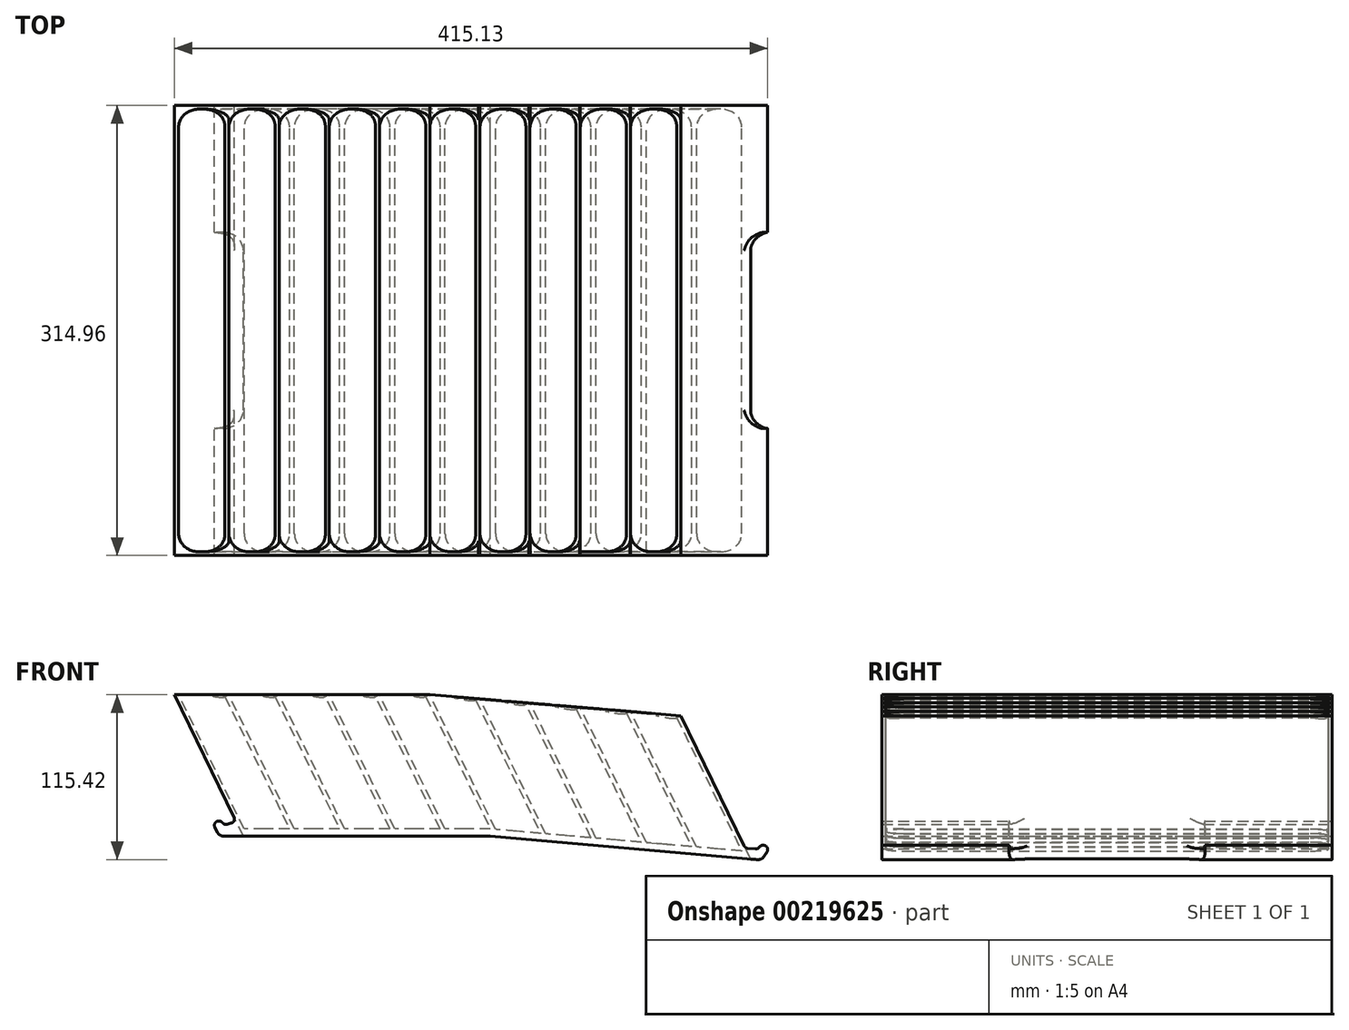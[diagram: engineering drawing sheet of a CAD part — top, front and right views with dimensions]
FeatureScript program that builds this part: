
annotation { "Feature Type Name" : "Feature", "Feature Type Description" : "" }
export const myFeature = defineFeature(function(context is Context, id is Id, definition is map)
    precondition{}
    {
        {
            var Q0;
            Q0=qCreatedBy(makeId("Front.planeOp"),FACE);
            var sketch = newSketch(context, id + "F0", { "sketchPlane" : qUnion([Q0])});
            skLineSegment(sketch, "E0", {"start": v(0, 0) * mm, "end": v(189.48, 0) * mm});
            skLineSegment(sketch, "E1", {"start": v(189.48, 0) * mm, "end": v(379.26, -16.6) * mm});
            skLineSegment(sketch, "E2", {"start": v(367.73, -8.25) * mm, "end": v(332.9, 63.16) * mm});
            skLineSegment(sketch, "E3", {"start": v(332.9, 63.16) * mm, "end": v(330.16, 61.83) * mm, "construction": true});
            skLineSegment(sketch, "E4", {"start": v(330.16, 61.83) * mm, "end": v(365.33, -10.29) * mm});
            skLineSegment(sketch, "E5", {"start": v(11.64, 10.16) * mm, "end": v(-21.71, 78.55) * mm});
            skLineSegment(sketch, "E6", {"start": v(-21.71, 78.55) * mm, "end": v(-18.66, 78.55) * mm});
            skLineSegment(sketch, "E7", {"start": v(-18.66, 78.55) * mm, "end": v(17.17, 5.08) * mm});
            skLineSegment(sketch, "E8", {"start": v(17.17, 5.08) * mm, "end": v(48.92, 5.08) * mm});
            skLineSegment(sketch, "E9", {"start": v(48.92, 5.08) * mm, "end": v(13.74, 77.21) * mm});
            skLineSegment(sketch, "E10", {"start": v(13.74, 77.21) * mm, "end": v(16.48, 78.55) * mm});
            skLineSegment(sketch, "E11", {"start": v(16.48, 78.55) * mm, "end": v(52.31, 5.08) * mm});
            skLineSegment(sketch, "E12", {"start": v(52.31, 5.08) * mm, "end": v(84.06, 5.08) * mm});
            skLineSegment(sketch, "E13", {"start": v(84.06, 5.08) * mm, "end": v(48.88, 77.21) * mm});
            skLineSegment(sketch, "E14", {"start": v(48.88, 77.21) * mm, "end": v(51.62, 78.55) * mm, "construction": true});
            skLineSegment(sketch, "E15", {"start": v(51.62, 78.55) * mm, "end": v(87.45, 5.08) * mm});
            skLineSegment(sketch, "E16", {"start": v(87.45, 5.08) * mm, "end": v(119.2, 5.08) * mm});
            skLineSegment(sketch, "E17", {"start": v(119.2, 5.08) * mm, "end": v(84.02, 77.21) * mm});
            skLineSegment(sketch, "E18", {"start": v(86.76, 78.55) * mm, "end": v(122.6, 5.08) * mm});
            skLineSegment(sketch, "E19", {"start": v(122.6, 5.08) * mm, "end": v(154.34, 5.08) * mm});
            skLineSegment(sketch, "E20", {"start": v(154.34, 5.08) * mm, "end": v(119.16, 77.21) * mm});
            skLineSegment(sketch, "E21", {"start": v(119.16, 77.21) * mm, "end": v(121.9, 78.55) * mm, "construction": true});
            skLineSegment(sketch, "E22", {"start": v(121.9, 78.55) * mm, "end": v(157.73, 5.08) * mm});
            skLineSegment(sketch, "E23", {"start": v(157.73, 5.08) * mm, "end": v(189.48, 5.08) * mm});
            skLineSegment(sketch, "E24", {"start": v(189.48, 0) * mm, "end": v(189.48, 5.08) * mm, "construction": true});
            skLineSegment(sketch, "E25", {"start": v(189.48, 5.08) * mm, "end": v(154.3, 77.21) * mm});
            skLineSegment(sketch, "E26", {"start": v(154.3, 77.21) * mm, "end": v(157.04, 78.55) * mm, "construction": true});
            skLineSegment(sketch, "E27", {"start": v(157.04, 78.55) * mm, "end": v(193.02, 4.8) * mm});
            skLineSegment(sketch, "E28", {"start": v(193.02, 4.8) * mm, "end": v(224.65, 2.02) * mm});
            skLineSegment(sketch, "E29", {"start": v(224.65, 2.02) * mm, "end": v(189.47, 74.14) * mm});
            skLineSegment(sketch, "E30", {"start": v(189.47, 74.14) * mm, "end": v(192.21, 75.47) * mm, "construction": true});
            skLineSegment(sketch, "E31", {"start": v(192.21, 75.47) * mm, "end": v(228.19, 1.71) * mm});
            skLineSegment(sketch, "E32", {"start": v(224.65, 2.02) * mm, "end": v(228.19, 1.71) * mm, "construction": true});
            skLineSegment(sketch, "E33", {"start": v(228.19, 1.71) * mm, "end": v(259.82, -1.05) * mm});
            skLineSegment(sketch, "E34", {"start": v(259.82, -1.05) * mm, "end": v(224.65, 71.06) * mm});
            skLineSegment(sketch, "E35", {"start": v(224.65, 71.06) * mm, "end": v(227.39, 72.4) * mm, "construction": true});
            skLineSegment(sketch, "E36", {"start": v(227.39, 72.4) * mm, "end": v(263.36, -1.36) * mm});
            skLineSegment(sketch, "E37", {"start": v(263.36, -1.36) * mm, "end": v(294.99, -4.13) * mm});
            skLineSegment(sketch, "E38", {"start": v(294.99, -4.13) * mm, "end": v(259.82, 67.98) * mm});
            skLineSegment(sketch, "E39", {"start": v(259.82, 67.98) * mm, "end": v(262.56, 69.32) * mm, "construction": true});
            skLineSegment(sketch, "E40", {"start": v(262.56, 69.32) * mm, "end": v(298.53, -4.44) * mm});
            skLineSegment(sketch, "E41", {"start": v(298.53, -4.44) * mm, "end": v(330.16, -7.2) * mm});
            skLineSegment(sketch, "E42", {"start": v(330.16, -7.2) * mm, "end": v(294.99, 64.9) * mm});
            skLineSegment(sketch, "E43", {"start": v(294.99, 64.9) * mm, "end": v(297.73, 66.24) * mm, "construction": true});
            skLineSegment(sketch, "E44", {"start": v(297.73, 66.24) * mm, "end": v(333.7, -7.52) * mm});
            skLineSegment(sketch, "E45", {"start": v(333.7, -7.52) * mm, "end": v(365.33, -10.29) * mm});
            skLineSegment(sketch, "E46", {"start": v(-18.66, 78.55) * mm, "end": v(157.04, 78.55) * mm, "construction": true});
            skLineSegment(sketch, "E47", {"start": v(157.04, 78.55) * mm, "end": v(332.9, 63.16) * mm, "construction": true});
            skLineSegment(sketch, "E48", {"start": v(84.02, 77.21) * mm, "end": v(86.76, 78.55) * mm, "construction": true});
            skLineSegment(sketch, "E49", {"start": v(367.73, -8.25) * mm, "end": v(376.94, -9.06) * mm});
            skLineSegment(sketch, "E50", {"start": v(379.26, -16.6) * mm, "end": v(383.77, -9.65) * mm});
            skArc(sketch, "E51", {"start": v(383.77, -9.65) * mm, "mid": v(380.63, -6.27) * mm, "end": v(376.94, -9.06) * mm});
            skLineSegment(sketch, "E52", {"start": v(376.94, -9.06) * mm, "end": v(383.77, -9.65) * mm, "construction": true});
            skLineSegment(sketch, "E53", {"start": v(0, 0) * mm, "end": v(-4.05, 7.62) * mm});
            skLineSegment(sketch, "E54", {"start": v(11.64, 10.16) * mm, "end": v(2.8, 7.62) * mm});
            skArc(sketch, "E55", {"start": v(2.8, 7.62) * mm, "mid": v(-0.62, 10.67) * mm, "end": v(-4.05, 7.62) * mm});
            skLineSegment(sketch, "E56", {"start": v(-4.05, 7.62) * mm, "end": v(2.8, 7.62) * mm, "construction": true});
            skLineSegment(sketch, "E57", {"start": v(-21.71, 78.55) * mm, "end": v(-31.72, 99.06) * mm});
            skLineSegment(sketch, "E58", {"start": v(-31.72, 99.06) * mm, "end": v(-28.67, 99.06) * mm});
            skLineSegment(sketch, "E59", {"start": v(-28.67, 99.06) * mm, "end": v(-18.66, 78.55) * mm});
            skLineSegment(sketch, "E60", {"start": v(13.74, 77.21) * mm, "end": v(3.73, 97.72) * mm});
            skLineSegment(sketch, "E61", {"start": v(3.73, 97.72) * mm, "end": v(6.47, 99.06) * mm});
            skLineSegment(sketch, "E62", {"start": v(6.47, 99.06) * mm, "end": v(16.48, 78.55) * mm});
            skLineSegment(sketch, "E63", {"start": v(48.88, 77.21) * mm, "end": v(38.87, 97.72) * mm});
            skLineSegment(sketch, "E64", {"start": v(38.87, 97.72) * mm, "end": v(41.61, 99.06) * mm});
            skLineSegment(sketch, "E65", {"start": v(41.61, 99.06) * mm, "end": v(51.62, 78.55) * mm});
            skLineSegment(sketch, "E66", {"start": v(109.16, 97.72) * mm, "end": v(111.9, 99.06) * mm});
            skLineSegment(sketch, "E67", {"start": v(259.82, 67.98) * mm, "end": v(249.49, 89.16) * mm});
            skLineSegment(sketch, "E68", {"start": v(249.49, 89.16) * mm, "end": v(252.23, 90.5) * mm});
            skLineSegment(sketch, "E69", {"start": v(252.23, 90.5) * mm, "end": v(262.56, 69.32) * mm});
            skLineSegment(sketch, "E70", {"start": v(330.16, 61.83) * mm, "end": v(319.83, 83) * mm});
            skLineSegment(sketch, "E71", {"start": v(319.83, 83) * mm, "end": v(322.57, 84.34) * mm});
            skLineSegment(sketch, "E72", {"start": v(322.57, 84.34) * mm, "end": v(332.9, 63.16) * mm});
            skLineSegment(sketch, "E73", {"start": v(154.3, 77.21) * mm, "end": v(144.3, 97.72) * mm});
            skLineSegment(sketch, "E74", {"start": v(294.99, 64.9) * mm, "end": v(284.66, 86.08) * mm});
            skLineSegment(sketch, "E75", {"start": v(189.47, 74.14) * mm, "end": v(179.15, 95.31) * mm});
            skLineSegment(sketch, "E76", {"start": v(-28.67, 99.06) * mm, "end": v(154.3, 99.06) * mm, "construction": true});
            skLineSegment(sketch, "E77", {"start": v(322.57, 84.34) * mm, "end": v(154.3, 99.06) * mm, "construction": true});
            skLineSegment(sketch, "E78", {"start": v(86.76, 78.55) * mm, "end": v(76.76, 99.06) * mm});
            skLineSegment(sketch, "E79", {"start": v(76.76, 99.06) * mm, "end": v(74.02, 97.72) * mm});
            skLineSegment(sketch, "E80", {"start": v(74.02, 97.72) * mm, "end": v(84.02, 77.21) * mm});
            skLineSegment(sketch, "E81", {"start": v(109.16, 97.72) * mm, "end": v(119.16, 77.21) * mm});
            skLineSegment(sketch, "E82", {"start": v(111.9, 99.06) * mm, "end": v(121.9, 78.55) * mm});
            skLineSegment(sketch, "E83", {"start": v(157.04, 78.55) * mm, "end": v(147.04, 99.06) * mm});
            skLineSegment(sketch, "E84", {"start": v(147.04, 99.06) * mm, "end": v(144.3, 97.72) * mm});
            skLineSegment(sketch, "E85", {"start": v(192.21, 75.47) * mm, "end": v(181.89, 96.65) * mm});
            skLineSegment(sketch, "E86", {"start": v(181.89, 96.65) * mm, "end": v(179.15, 95.31) * mm});
            skLineSegment(sketch, "E87", {"start": v(227.39, 72.4) * mm, "end": v(217.06, 93.57) * mm});
            skLineSegment(sketch, "E88", {"start": v(217.06, 93.57) * mm, "end": v(214.32, 92.23) * mm});
            skLineSegment(sketch, "E89", {"start": v(214.32, 92.23) * mm, "end": v(224.65, 71.06) * mm});
            skLineSegment(sketch, "E90", {"start": v(297.73, 66.24) * mm, "end": v(287.4, 87.42) * mm});
            skLineSegment(sketch, "E91", {"start": v(287.4, 87.42) * mm, "end": v(284.66, 86.08) * mm});
            skSolve(sketch);
        }
        {
            var Q0;
            Q0 = qSketchRegion(id + "F0", true);
            extrude(context, id + "F1", {"entities" : qUnion([Q0]), "endBound" : BoundingType.SYMMETRIC, "depth" : 314.96 * mm});
        }
        {
            var Q0;
            Q0=makeQuery(id+"F1.opExtrude","SWEPT_EDGE",EDGE,{"disambiguationData":[OSD([sQuery(id+"F0.wireOp",EDGE,"E5"),sQuery(id+"F0.wireOp",EDGE,"E54")])]});
            var Q1;
            Q1=makeQuery(id+"F1.opExtrude","SWEPT_EDGE",EDGE,{"disambiguationData":[OSD([sQuery(id+"F0.wireOp",EDGE,"E54"),sQuery(id+"F0.wireOp",EDGE,"E55")])]});
            var Q2;
            Q2=makeQuery(id+"F1.opExtrude","SWEPT_EDGE",EDGE,{"disambiguationData":[OSD([sQuery(id+"F0.wireOp",EDGE,"E2"),sQuery(id+"F0.wireOp",EDGE,"E49")])]});
            var Q3;
            Q3=makeQuery(id+"F1.opExtrude","SWEPT_EDGE",EDGE,{"disambiguationData":[OSD([sQuery(id+"F0.wireOp",EDGE,"E49"),sQuery(id+"F0.wireOp",EDGE,"E51")])]});
            var Q4;
            Q4=makeQuery(id+"F1.opExtrude","SWEPT_EDGE",EDGE,{"disambiguationData":[OSD([sQuery(id+"F0.wireOp",EDGE,"E50"),sQuery(id+"F0.wireOp",EDGE,"E51")])]});
            var Q5;
            Q5=makeQuery(id+"F1.opExtrude","SWEPT_EDGE",EDGE,{"disambiguationData":[OSD([sQuery(id+"F0.wireOp",EDGE,"E53"),sQuery(id+"F0.wireOp",EDGE,"E55")])]});
            fillet(context, id + "F2", {"entities" : qUnion([Q0, Q1, Q2, Q3, Q4, Q5]), "radius" : 3.05 * mm, "tangentPropagation" : true, "allowEdgeOverflow" : false});
        }
        {
            var Q0;
            Q0=makeQuery(id+"F1.opExtrude","SWEPT_EDGE",EDGE,{"disambiguationData":[OSD([sQuery(id+"F0.wireOp",EDGE,"E0"),sQuery(id+"F0.wireOp",EDGE,"E53")])]});
            var Q1;
            Q1=makeQuery(id+"F1.opExtrude","SWEPT_EDGE",EDGE,{"disambiguationData":[OSD([sQuery(id+"F0.wireOp",EDGE,"E1"),sQuery(id+"F0.wireOp",EDGE,"E50")])]});
            fillet(context, id + "F3", {"entities" : qUnion([Q0, Q1]), "radius" : 5.08 * mm, "tangentPropagation" : true, "allowEdgeOverflow" : false});
        }
        {
            var Q0;
            Q0=makeQuery(id+"F1.opExtrude","CAP_FACE",FACE,{"disambiguationData":[OSD([sQuery(id+"F0.wireOp",EDGE,"E0"),sQuery(id+"F0.wireOp",EDGE,"E1"),sQuery(id+"F0.wireOp",EDGE,"E2"),sQuery(id+"F0.wireOp",EDGE,"E3"),sQuery(id+"F0.wireOp",EDGE,"E4"),sQuery(id+"F0.wireOp",EDGE,"E5"),sQuery(id+"F0.wireOp",EDGE,"E6"),sQuery(id+"F0.wireOp",EDGE,"E7"),sQuery(id+"F0.wireOp",EDGE,"E8"),sQuery(id+"F0.wireOp",EDGE,"E9"),sQuery(id+"F0.wireOp",EDGE,"E10"),sQuery(id+"F0.wireOp",EDGE,"E11"),sQuery(id+"F0.wireOp",EDGE,"E12"),sQuery(id+"F0.wireOp",EDGE,"E13"),sQuery(id+"F0.wireOp",EDGE,"E14"),sQuery(id+"F0.wireOp",EDGE,"E15"),sQuery(id+"F0.wireOp",EDGE,"E16"),sQuery(id+"F0.wireOp",EDGE,"E17"),sQuery(id+"F0.wireOp",EDGE,"E18"),sQuery(id+"F0.wireOp",EDGE,"E19"),sQuery(id+"F0.wireOp",EDGE,"E20"),sQuery(id+"F0.wireOp",EDGE,"E21"),sQuery(id+"F0.wireOp",EDGE,"E22"),sQuery(id+"F0.wireOp",EDGE,"E23"),sQuery(id+"F0.wireOp",EDGE,"E25"),sQuery(id+"F0.wireOp",EDGE,"E26"),sQuery(id+"F0.wireOp",EDGE,"E27"),sQuery(id+"F0.wireOp",EDGE,"E28"),sQuery(id+"F0.wireOp",EDGE,"E29"),sQuery(id+"F0.wireOp",EDGE,"E30"),sQuery(id+"F0.wireOp",EDGE,"E31"),sQuery(id+"F0.wireOp",EDGE,"E33"),sQuery(id+"F0.wireOp",EDGE,"E34"),sQuery(id+"F0.wireOp",EDGE,"E35"),sQuery(id+"F0.wireOp",EDGE,"E36"),sQuery(id+"F0.wireOp",EDGE,"E37"),sQuery(id+"F0.wireOp",EDGE,"E38"),sQuery(id+"F0.wireOp",EDGE,"E39"),sQuery(id+"F0.wireOp",EDGE,"E40"),sQuery(id+"F0.wireOp",EDGE,"E41"),sQuery(id+"F0.wireOp",EDGE,"E42"),sQuery(id+"F0.wireOp",EDGE,"E43"),sQuery(id+"F0.wireOp",EDGE,"E44"),sQuery(id+"F0.wireOp",EDGE,"E45"),sQuery(id+"F0.wireOp",EDGE,"E48"),sQuery(id+"F0.wireOp",EDGE,"E49"),sQuery(id+"F0.wireOp",EDGE,"E50"),sQuery(id+"F0.wireOp",EDGE,"E51"),sQuery(id+"F0.wireOp",EDGE,"E53"),sQuery(id+"F0.wireOp",EDGE,"E54"),sQuery(id+"F0.wireOp",EDGE,"E55")])],"isStart":false});
            var sketch = newSketch(context, id + "F4", { "sketchPlane" : qUnion([Q0])});
            skLineSegment(sketch, "E92.0", {"start": v(10.05, 13.42) * mm, "end": v(-31.72, 99.06) * mm});
            skArc(sketch, "E92.1", {"start": v(10.05, 13.42) * mm, "mid": v(10.1, 10.85) * mm, "end": v(8.15, 9.16) * mm});
            skLineSegment(sketch, "E92.2", {"start": v(8.15, 9.16) * mm, "end": v(5.3, 8.34) * mm});
            skArc(sketch, "E92.3", {"start": v(5.3, 8.34) * mm, "mid": v(3.53, 8.36) * mm, "end": v(2.08, 9.37) * mm});
            skArc(sketch, "E92.4", {"start": v(2.08, 9.37) * mm, "mid": v(0.97, 10.28) * mm, "end": v(-0.42, 10.66) * mm});
            skArc(sketch, "E92.5", {"start": v(-0.42, 10.66) * mm, "mid": v(-3.17, 9.26) * mm, "end": v(-3.3, 6.19) * mm});
            skLineSegment(sketch, "E92.6", {"start": v(-1.43, 2.7) * mm, "end": v(-3.3, 6.19) * mm});
            skArc(sketch, "E92.7", {"start": v(-1.43, 2.7) * mm, "mid": v(0.44, 0.73) * mm, "end": v(3.05, 0) * mm});
            skLineSegment(sketch, "E92.8", {"start": v(3.05, 0) * mm, "end": v(189.48, 0) * mm});
            skLineSegment(sketch, "E92.9", {"start": v(189.48, 0) * mm, "end": v(376.22, -16.34) * mm});
            skLineSegment(sketch, "E92.10", {"start": v(366.98, -6.7) * mm, "end": v(322.57, 84.34) * mm});
            skArc(sketch, "E92.11", {"start": v(369.45, -8.4) * mm, "mid": v(367.99, -7.88) * mm, "end": v(366.98, -6.7) * mm});
            skLineSegment(sketch, "E92.12", {"start": v(369.45, -8.4) * mm, "end": v(374.84, -8.87) * mm});
            skArc(sketch, "E92.13", {"start": v(377.56, -7.65) * mm, "mid": v(376.36, -8.62) * mm, "end": v(374.84, -8.87) * mm});
            skArc(sketch, "E92.14", {"start": v(380.66, -6.27) * mm, "mid": v(378.93, -6.55) * mm, "end": v(377.56, -7.65) * mm});
            skArc(sketch, "E92.15", {"start": v(382.92, -10.97) * mm, "mid": v(383.1, -7.98) * mm, "end": v(380.66, -6.27) * mm});
            skLineSegment(sketch, "E92.16", {"start": v(380.92, -14.04) * mm, "end": v(382.92, -10.97) * mm});
            skArc(sketch, "E92.17", {"start": v(376.22, -16.34) * mm, "mid": v(378.89, -15.84) * mm, "end": v(380.92, -14.04) * mm});
            skLineSegment(sketch, "E93", {"start": v(322.57, 84.34) * mm, "end": v(147.04, 99.06) * mm});
            skLineSegment(sketch, "E94", {"start": v(147.04, 99.06) * mm, "end": v(-31.72, 99.06) * mm});
            skSolve(sketch);
        }
        {
            var Q0;
            Q0 = qSketchRegion(id + "F4", true);
            extrude(context, id + "F5", {"entities" : qUnion([Q0]), "oppositeDirection" : true, "depth" : 2.54 * mm});
        }
        {
            var Q0;
            Q0=makeQuery(id+"F5.opExtrude","SWEPT_BODY",BODY,{"disambiguationData":[OSD([sQuery(id+"F4.wireOp",EDGE,"E92.0"),sQuery(id+"F4.wireOp",EDGE,"E92.1"),sQuery(id+"F4.wireOp",EDGE,"E92.2"),sQuery(id+"F4.wireOp",EDGE,"E92.3"),sQuery(id+"F4.wireOp",EDGE,"E92.4"),sQuery(id+"F4.wireOp",EDGE,"E92.5"),sQuery(id+"F4.wireOp",EDGE,"E92.6"),sQuery(id+"F4.wireOp",EDGE,"E92.7"),sQuery(id+"F4.wireOp",EDGE,"E92.8"),sQuery(id+"F4.wireOp",EDGE,"E92.9"),sQuery(id+"F4.wireOp",EDGE,"E92.10"),sQuery(id+"F4.wireOp",EDGE,"E92.11"),sQuery(id+"F4.wireOp",EDGE,"E92.12"),sQuery(id+"F4.wireOp",EDGE,"E92.13"),sQuery(id+"F4.wireOp",EDGE,"E92.14"),sQuery(id+"F4.wireOp",EDGE,"E92.15"),sQuery(id+"F4.wireOp",EDGE,"E92.16"),sQuery(id+"F4.wireOp",EDGE,"E92.17"),sQuery(id+"F4.wireOp",EDGE,"E93"),sQuery(id+"F4.wireOp",EDGE,"E94")])]});
            var Q1;
            Q1=qCreatedBy(makeId("Front.planeOp"),FACE);
            mirror(context, id + "F6", {"operationType" : NewBodyOperationType.ADD, "entities" : qUnion([Q0]), "mirrorPlane" : qUnion([Q1])});
        }
        {
            var Q0;
            Q0=makeQuery(id+"F1.opExtrude","SWEPT_FACE",FACE,{"disambiguationData":[OSD([sQuery(id+"F0.wireOp",EDGE,"E61")])]});
            var sketch = newSketch(context, id + "F7", { "sketchPlane" : qUnion([Q0])});
            skLineSegment(sketch, "E95.bottom", {"start": v(14.92, -68.58) * mm, "end": v(-14.92, -68.58) * mm});
            skLineSegment(sketch, "E95.top", {"start": v(14.92, 68.58) * mm, "end": v(-14.92, 68.58) * mm});
            skLineSegment(sketch, "E95.left", {"start": v(14.92, -68.58) * mm, "end": v(14.92, 68.58) * mm});
            skLineSegment(sketch, "E95.right", {"start": v(-14.92, -68.58) * mm, "end": v(-14.92, 68.58) * mm});
            skPoint(sketch, "E95.middle", {"position": v(0, 0) * mm});
            skSolve(sketch);
        }
        {
            var Q0;
            Q0 = qSketchRegion(id + "F7", true);
            extrude(context, id + "F8", {"entities" : qUnion([Q0]), "operationType" : NewBodyOperationType.REMOVE, "oppositeDirection" : true, "depth" : 144.78 * mm});
        }
        {
            var Q0;
            Q0=makeQuery(id+"F1.opExtrude","SWEPT_FACE",FACE,{"disambiguationData":[OSD([sQuery(id+"F0.wireOp",EDGE,"E61")])]});
            var sketch = newSketch(context, id + "F9", { "sketchPlane" : qUnion([Q0])});
            skLineSegment(sketch, "E96.bottom", {"start": v(326.9, -68.58) * mm, "end": v(466.95, -68.58) * mm});
            skLineSegment(sketch, "E96.top", {"start": v(326.9, 68.58) * mm, "end": v(466.95, 68.58) * mm});
            skLineSegment(sketch, "E96.left", {"start": v(326.9, -68.58) * mm, "end": v(326.9, 68.58) * mm});
            skLineSegment(sketch, "E96.right", {"start": v(466.95, -68.58) * mm, "end": v(466.95, 68.58) * mm});
            skPoint(sketch, "E96.middle", {"position": v(396.93, 0) * mm});
            skSolve(sketch);
        }
        {
            var Q0;
            Q0 = qSketchRegion(id + "F9", true);
            extrude(context, id + "F10", {"entities" : qUnion([Q0]), "operationType" : NewBodyOperationType.REMOVE, "oppositeDirection" : true, "depth" : 293.12 * mm});
        }
        {
            var Q0;
            Q0=makeQuery(id+"F10.boolean.opBoolean","COPY",EDGE,{"derivedFrom":makeQuery(id+"F10.opExtrude","SWEPT_EDGE",EDGE,{"disambiguationData":[OSD([sQuery(id+"F9.wireOp",EDGE,"E96.bottom"),sQuery(id+"F9.wireOp",EDGE,"E96.left")])]})});
            var Q1;
            Q1=makeQuery(id+"F10.boolean.opBoolean","COPY",EDGE,{"derivedFrom":makeQuery(id+"F10.opExtrude","SWEPT_EDGE",EDGE,{"disambiguationData":[OSD([sQuery(id+"F9.wireOp",EDGE,"E96.top"),sQuery(id+"F9.wireOp",EDGE,"E96.left")])]})});
            var Q2;
            Q2=makeQuery(id+"F8.boolean.opBoolean","COPY",EDGE,{"derivedFrom":makeQuery(id+"F8.opExtrude","SWEPT_EDGE",EDGE,{"disambiguationData":[OSD([sQuery(id+"F7.wireOp",EDGE,"E95.top"),sQuery(id+"F7.wireOp",EDGE,"E95.left")])]})});
            var Q3;
            Q3=makeQuery(id+"F8.boolean.opBoolean","COPY",EDGE,{"derivedFrom":makeQuery(id+"F8.opExtrude","SWEPT_EDGE",EDGE,{"disambiguationData":[OSD([sQuery(id+"F7.wireOp",EDGE,"E95.bottom"),sQuery(id+"F7.wireOp",EDGE,"E95.left")])]})});
            fillet(context, id + "F11", {"entities" : qUnion([Q0, Q1, Q2, Q3]), "radius" : 12.7 * mm, "tangentPropagation" : true, "allowEdgeOverflow" : false});
        }
        {
            var Q0;
            Q0=makeQuery(id+"F6.boolean.opBoolean","INTERSECT",EDGE,{"derivedFrom":[makeQuery(id+"F1.opExtrude","SWEPT_FACE",FACE,{"disambiguationData":[OSD([sQuery(id+"F0.wireOp",EDGE,"E29"),sQuery(id+"F0.wireOp",EDGE,"E75")])]}),makeQuery(id+"F5.opExtrude","CAP_FACE",FACE,{"disambiguationData":[OSD([sQuery(id+"F4.wireOp",EDGE,"E92.0"),sQuery(id+"F4.wireOp",EDGE,"E92.1"),sQuery(id+"F4.wireOp",EDGE,"E92.2"),sQuery(id+"F4.wireOp",EDGE,"E92.3"),sQuery(id+"F4.wireOp",EDGE,"E92.4"),sQuery(id+"F4.wireOp",EDGE,"E92.5"),sQuery(id+"F4.wireOp",EDGE,"E92.6"),sQuery(id+"F4.wireOp",EDGE,"E92.7"),sQuery(id+"F4.wireOp",EDGE,"E92.8"),sQuery(id+"F4.wireOp",EDGE,"E92.9"),sQuery(id+"F4.wireOp",EDGE,"E92.10"),sQuery(id+"F4.wireOp",EDGE,"E92.11"),sQuery(id+"F4.wireOp",EDGE,"E92.12"),sQuery(id+"F4.wireOp",EDGE,"E92.13"),sQuery(id+"F4.wireOp",EDGE,"E92.14"),sQuery(id+"F4.wireOp",EDGE,"E92.15"),sQuery(id+"F4.wireOp",EDGE,"E92.16"),sQuery(id+"F4.wireOp",EDGE,"E92.17"),sQuery(id+"F4.wireOp",EDGE,"E93"),sQuery(id+"F4.wireOp",EDGE,"E94")])],"isStart":false})]});
            var Q1;
            Q1=makeQuery(id+"F6.boolean.opBoolean","INTERSECT",EDGE,{"derivedFrom":[makeQuery(id+"F1.opExtrude","SWEPT_FACE",FACE,{"disambiguationData":[OSD([sQuery(id+"F0.wireOp",EDGE,"E27"),sQuery(id+"F0.wireOp",EDGE,"E83")])]}),makeQuery(id+"F5.opExtrude","CAP_FACE",FACE,{"disambiguationData":[OSD([sQuery(id+"F4.wireOp",EDGE,"E92.0"),sQuery(id+"F4.wireOp",EDGE,"E92.1"),sQuery(id+"F4.wireOp",EDGE,"E92.2"),sQuery(id+"F4.wireOp",EDGE,"E92.3"),sQuery(id+"F4.wireOp",EDGE,"E92.4"),sQuery(id+"F4.wireOp",EDGE,"E92.5"),sQuery(id+"F4.wireOp",EDGE,"E92.6"),sQuery(id+"F4.wireOp",EDGE,"E92.7"),sQuery(id+"F4.wireOp",EDGE,"E92.8"),sQuery(id+"F4.wireOp",EDGE,"E92.9"),sQuery(id+"F4.wireOp",EDGE,"E92.10"),sQuery(id+"F4.wireOp",EDGE,"E92.11"),sQuery(id+"F4.wireOp",EDGE,"E92.12"),sQuery(id+"F4.wireOp",EDGE,"E92.13"),sQuery(id+"F4.wireOp",EDGE,"E92.14"),sQuery(id+"F4.wireOp",EDGE,"E92.15"),sQuery(id+"F4.wireOp",EDGE,"E92.16"),sQuery(id+"F4.wireOp",EDGE,"E92.17"),sQuery(id+"F4.wireOp",EDGE,"E93"),sQuery(id+"F4.wireOp",EDGE,"E94")])],"isStart":false})]});
            var Q2;
            Q2=makeQuery(id+"F6.boolean.opBoolean","INTERSECT",EDGE,{"derivedFrom":[makeQuery(id+"F1.opExtrude","SWEPT_FACE",FACE,{"disambiguationData":[OSD([sQuery(id+"F0.wireOp",EDGE,"E25"),sQuery(id+"F0.wireOp",EDGE,"E73")])]}),makeQuery(id+"F5.opExtrude","CAP_FACE",FACE,{"disambiguationData":[OSD([sQuery(id+"F4.wireOp",EDGE,"E92.0"),sQuery(id+"F4.wireOp",EDGE,"E92.1"),sQuery(id+"F4.wireOp",EDGE,"E92.2"),sQuery(id+"F4.wireOp",EDGE,"E92.3"),sQuery(id+"F4.wireOp",EDGE,"E92.4"),sQuery(id+"F4.wireOp",EDGE,"E92.5"),sQuery(id+"F4.wireOp",EDGE,"E92.6"),sQuery(id+"F4.wireOp",EDGE,"E92.7"),sQuery(id+"F4.wireOp",EDGE,"E92.8"),sQuery(id+"F4.wireOp",EDGE,"E92.9"),sQuery(id+"F4.wireOp",EDGE,"E92.10"),sQuery(id+"F4.wireOp",EDGE,"E92.11"),sQuery(id+"F4.wireOp",EDGE,"E92.12"),sQuery(id+"F4.wireOp",EDGE,"E92.13"),sQuery(id+"F4.wireOp",EDGE,"E92.14"),sQuery(id+"F4.wireOp",EDGE,"E92.15"),sQuery(id+"F4.wireOp",EDGE,"E92.16"),sQuery(id+"F4.wireOp",EDGE,"E92.17"),sQuery(id+"F4.wireOp",EDGE,"E93"),sQuery(id+"F4.wireOp",EDGE,"E94")])],"isStart":false})]});
            var Q3;
            Q3=makeQuery(id+"F6.boolean.opBoolean","INTERSECT",EDGE,{"derivedFrom":[makeQuery(id+"F1.opExtrude","SWEPT_FACE",FACE,{"disambiguationData":[OSD([sQuery(id+"F0.wireOp",EDGE,"E22"),sQuery(id+"F0.wireOp",EDGE,"E82")])]}),makeQuery(id+"F5.opExtrude","CAP_FACE",FACE,{"disambiguationData":[OSD([sQuery(id+"F4.wireOp",EDGE,"E92.0"),sQuery(id+"F4.wireOp",EDGE,"E92.1"),sQuery(id+"F4.wireOp",EDGE,"E92.2"),sQuery(id+"F4.wireOp",EDGE,"E92.3"),sQuery(id+"F4.wireOp",EDGE,"E92.4"),sQuery(id+"F4.wireOp",EDGE,"E92.5"),sQuery(id+"F4.wireOp",EDGE,"E92.6"),sQuery(id+"F4.wireOp",EDGE,"E92.7"),sQuery(id+"F4.wireOp",EDGE,"E92.8"),sQuery(id+"F4.wireOp",EDGE,"E92.9"),sQuery(id+"F4.wireOp",EDGE,"E92.10"),sQuery(id+"F4.wireOp",EDGE,"E92.11"),sQuery(id+"F4.wireOp",EDGE,"E92.12"),sQuery(id+"F4.wireOp",EDGE,"E92.13"),sQuery(id+"F4.wireOp",EDGE,"E92.14"),sQuery(id+"F4.wireOp",EDGE,"E92.15"),sQuery(id+"F4.wireOp",EDGE,"E92.16"),sQuery(id+"F4.wireOp",EDGE,"E92.17"),sQuery(id+"F4.wireOp",EDGE,"E93"),sQuery(id+"F4.wireOp",EDGE,"E94")])],"isStart":false})]});
            var Q4;
            Q4=makeQuery(id+"F6.boolean.opBoolean","INTERSECT",EDGE,{"derivedFrom":[makeQuery(id+"F1.opExtrude","SWEPT_FACE",FACE,{"disambiguationData":[OSD([sQuery(id+"F0.wireOp",EDGE,"E20"),sQuery(id+"F0.wireOp",EDGE,"E81")])]}),makeQuery(id+"F5.opExtrude","CAP_FACE",FACE,{"disambiguationData":[OSD([sQuery(id+"F4.wireOp",EDGE,"E92.0"),sQuery(id+"F4.wireOp",EDGE,"E92.1"),sQuery(id+"F4.wireOp",EDGE,"E92.2"),sQuery(id+"F4.wireOp",EDGE,"E92.3"),sQuery(id+"F4.wireOp",EDGE,"E92.4"),sQuery(id+"F4.wireOp",EDGE,"E92.5"),sQuery(id+"F4.wireOp",EDGE,"E92.6"),sQuery(id+"F4.wireOp",EDGE,"E92.7"),sQuery(id+"F4.wireOp",EDGE,"E92.8"),sQuery(id+"F4.wireOp",EDGE,"E92.9"),sQuery(id+"F4.wireOp",EDGE,"E92.10"),sQuery(id+"F4.wireOp",EDGE,"E92.11"),sQuery(id+"F4.wireOp",EDGE,"E92.12"),sQuery(id+"F4.wireOp",EDGE,"E92.13"),sQuery(id+"F4.wireOp",EDGE,"E92.14"),sQuery(id+"F4.wireOp",EDGE,"E92.15"),sQuery(id+"F4.wireOp",EDGE,"E92.16"),sQuery(id+"F4.wireOp",EDGE,"E92.17"),sQuery(id+"F4.wireOp",EDGE,"E93"),sQuery(id+"F4.wireOp",EDGE,"E94")])],"isStart":false})]});
            var Q5;
            Q5=makeQuery(id+"F6.boolean.opBoolean","INTERSECT",EDGE,{"derivedFrom":[makeQuery(id+"F1.opExtrude","SWEPT_FACE",FACE,{"disambiguationData":[OSD([sQuery(id+"F0.wireOp",EDGE,"E18"),sQuery(id+"F0.wireOp",EDGE,"E78")])]}),makeQuery(id+"F5.opExtrude","CAP_FACE",FACE,{"disambiguationData":[OSD([sQuery(id+"F4.wireOp",EDGE,"E92.0"),sQuery(id+"F4.wireOp",EDGE,"E92.1"),sQuery(id+"F4.wireOp",EDGE,"E92.2"),sQuery(id+"F4.wireOp",EDGE,"E92.3"),sQuery(id+"F4.wireOp",EDGE,"E92.4"),sQuery(id+"F4.wireOp",EDGE,"E92.5"),sQuery(id+"F4.wireOp",EDGE,"E92.6"),sQuery(id+"F4.wireOp",EDGE,"E92.7"),sQuery(id+"F4.wireOp",EDGE,"E92.8"),sQuery(id+"F4.wireOp",EDGE,"E92.9"),sQuery(id+"F4.wireOp",EDGE,"E92.10"),sQuery(id+"F4.wireOp",EDGE,"E92.11"),sQuery(id+"F4.wireOp",EDGE,"E92.12"),sQuery(id+"F4.wireOp",EDGE,"E92.13"),sQuery(id+"F4.wireOp",EDGE,"E92.14"),sQuery(id+"F4.wireOp",EDGE,"E92.15"),sQuery(id+"F4.wireOp",EDGE,"E92.16"),sQuery(id+"F4.wireOp",EDGE,"E92.17"),sQuery(id+"F4.wireOp",EDGE,"E93"),sQuery(id+"F4.wireOp",EDGE,"E94")])],"isStart":false})]});
            var Q6;
            Q6=makeQuery(id+"F6.boolean.opBoolean","INTERSECT",EDGE,{"derivedFrom":[makeQuery(id+"F1.opExtrude","SWEPT_FACE",FACE,{"disambiguationData":[OSD([sQuery(id+"F0.wireOp",EDGE,"E17"),sQuery(id+"F0.wireOp",EDGE,"E80")])]}),makeQuery(id+"F5.opExtrude","CAP_FACE",FACE,{"disambiguationData":[OSD([sQuery(id+"F4.wireOp",EDGE,"E92.0"),sQuery(id+"F4.wireOp",EDGE,"E92.1"),sQuery(id+"F4.wireOp",EDGE,"E92.2"),sQuery(id+"F4.wireOp",EDGE,"E92.3"),sQuery(id+"F4.wireOp",EDGE,"E92.4"),sQuery(id+"F4.wireOp",EDGE,"E92.5"),sQuery(id+"F4.wireOp",EDGE,"E92.6"),sQuery(id+"F4.wireOp",EDGE,"E92.7"),sQuery(id+"F4.wireOp",EDGE,"E92.8"),sQuery(id+"F4.wireOp",EDGE,"E92.9"),sQuery(id+"F4.wireOp",EDGE,"E92.10"),sQuery(id+"F4.wireOp",EDGE,"E92.11"),sQuery(id+"F4.wireOp",EDGE,"E92.12"),sQuery(id+"F4.wireOp",EDGE,"E92.13"),sQuery(id+"F4.wireOp",EDGE,"E92.14"),sQuery(id+"F4.wireOp",EDGE,"E92.15"),sQuery(id+"F4.wireOp",EDGE,"E92.16"),sQuery(id+"F4.wireOp",EDGE,"E92.17"),sQuery(id+"F4.wireOp",EDGE,"E93"),sQuery(id+"F4.wireOp",EDGE,"E94")])],"isStart":false})]});
            var Q7;
            Q7=makeQuery(id+"F6.boolean.opBoolean","INTERSECT",EDGE,{"derivedFrom":[makeQuery(id+"F1.opExtrude","SWEPT_FACE",FACE,{"disambiguationData":[OSD([sQuery(id+"F0.wireOp",EDGE,"E15"),sQuery(id+"F0.wireOp",EDGE,"E65")])]}),makeQuery(id+"F5.opExtrude","CAP_FACE",FACE,{"disambiguationData":[OSD([sQuery(id+"F4.wireOp",EDGE,"E92.0"),sQuery(id+"F4.wireOp",EDGE,"E92.1"),sQuery(id+"F4.wireOp",EDGE,"E92.2"),sQuery(id+"F4.wireOp",EDGE,"E92.3"),sQuery(id+"F4.wireOp",EDGE,"E92.4"),sQuery(id+"F4.wireOp",EDGE,"E92.5"),sQuery(id+"F4.wireOp",EDGE,"E92.6"),sQuery(id+"F4.wireOp",EDGE,"E92.7"),sQuery(id+"F4.wireOp",EDGE,"E92.8"),sQuery(id+"F4.wireOp",EDGE,"E92.9"),sQuery(id+"F4.wireOp",EDGE,"E92.10"),sQuery(id+"F4.wireOp",EDGE,"E92.11"),sQuery(id+"F4.wireOp",EDGE,"E92.12"),sQuery(id+"F4.wireOp",EDGE,"E92.13"),sQuery(id+"F4.wireOp",EDGE,"E92.14"),sQuery(id+"F4.wireOp",EDGE,"E92.15"),sQuery(id+"F4.wireOp",EDGE,"E92.16"),sQuery(id+"F4.wireOp",EDGE,"E92.17"),sQuery(id+"F4.wireOp",EDGE,"E93"),sQuery(id+"F4.wireOp",EDGE,"E94")])],"isStart":false})]});
            var Q8;
            Q8=makeQuery(id+"F6.boolean.opBoolean","INTERSECT",EDGE,{"derivedFrom":[makeQuery(id+"F1.opExtrude","SWEPT_FACE",FACE,{"disambiguationData":[OSD([sQuery(id+"F0.wireOp",EDGE,"E13"),sQuery(id+"F0.wireOp",EDGE,"E63")])]}),makeQuery(id+"F5.opExtrude","CAP_FACE",FACE,{"disambiguationData":[OSD([sQuery(id+"F4.wireOp",EDGE,"E92.0"),sQuery(id+"F4.wireOp",EDGE,"E92.1"),sQuery(id+"F4.wireOp",EDGE,"E92.2"),sQuery(id+"F4.wireOp",EDGE,"E92.3"),sQuery(id+"F4.wireOp",EDGE,"E92.4"),sQuery(id+"F4.wireOp",EDGE,"E92.5"),sQuery(id+"F4.wireOp",EDGE,"E92.6"),sQuery(id+"F4.wireOp",EDGE,"E92.7"),sQuery(id+"F4.wireOp",EDGE,"E92.8"),sQuery(id+"F4.wireOp",EDGE,"E92.9"),sQuery(id+"F4.wireOp",EDGE,"E92.10"),sQuery(id+"F4.wireOp",EDGE,"E92.11"),sQuery(id+"F4.wireOp",EDGE,"E92.12"),sQuery(id+"F4.wireOp",EDGE,"E92.13"),sQuery(id+"F4.wireOp",EDGE,"E92.14"),sQuery(id+"F4.wireOp",EDGE,"E92.15"),sQuery(id+"F4.wireOp",EDGE,"E92.16"),sQuery(id+"F4.wireOp",EDGE,"E92.17"),sQuery(id+"F4.wireOp",EDGE,"E93"),sQuery(id+"F4.wireOp",EDGE,"E94")])],"isStart":false})]});
            var Q9;
            Q9=makeQuery(id+"F6.boolean.opBoolean","INTERSECT",EDGE,{"derivedFrom":[makeQuery(id+"F1.opExtrude","SWEPT_FACE",FACE,{"disambiguationData":[OSD([sQuery(id+"F0.wireOp",EDGE,"E11"),sQuery(id+"F0.wireOp",EDGE,"E62")])]}),makeQuery(id+"F5.opExtrude","CAP_FACE",FACE,{"disambiguationData":[OSD([sQuery(id+"F4.wireOp",EDGE,"E92.0"),sQuery(id+"F4.wireOp",EDGE,"E92.1"),sQuery(id+"F4.wireOp",EDGE,"E92.2"),sQuery(id+"F4.wireOp",EDGE,"E92.3"),sQuery(id+"F4.wireOp",EDGE,"E92.4"),sQuery(id+"F4.wireOp",EDGE,"E92.5"),sQuery(id+"F4.wireOp",EDGE,"E92.6"),sQuery(id+"F4.wireOp",EDGE,"E92.7"),sQuery(id+"F4.wireOp",EDGE,"E92.8"),sQuery(id+"F4.wireOp",EDGE,"E92.9"),sQuery(id+"F4.wireOp",EDGE,"E92.10"),sQuery(id+"F4.wireOp",EDGE,"E92.11"),sQuery(id+"F4.wireOp",EDGE,"E92.12"),sQuery(id+"F4.wireOp",EDGE,"E92.13"),sQuery(id+"F4.wireOp",EDGE,"E92.14"),sQuery(id+"F4.wireOp",EDGE,"E92.15"),sQuery(id+"F4.wireOp",EDGE,"E92.16"),sQuery(id+"F4.wireOp",EDGE,"E92.17"),sQuery(id+"F4.wireOp",EDGE,"E93"),sQuery(id+"F4.wireOp",EDGE,"E94")])],"isStart":false})]});
            var Q10;
            Q10=makeQuery(id+"F6.boolean.opBoolean","INTERSECT",EDGE,{"derivedFrom":[makeQuery(id+"F1.opExtrude","SWEPT_FACE",FACE,{"disambiguationData":[OSD([sQuery(id+"F0.wireOp",EDGE,"E7"),sQuery(id+"F0.wireOp",EDGE,"E59")])]}),makeQuery(id+"F5.opExtrude","CAP_FACE",FACE,{"disambiguationData":[OSD([sQuery(id+"F4.wireOp",EDGE,"E92.0"),sQuery(id+"F4.wireOp",EDGE,"E92.1"),sQuery(id+"F4.wireOp",EDGE,"E92.2"),sQuery(id+"F4.wireOp",EDGE,"E92.3"),sQuery(id+"F4.wireOp",EDGE,"E92.4"),sQuery(id+"F4.wireOp",EDGE,"E92.5"),sQuery(id+"F4.wireOp",EDGE,"E92.6"),sQuery(id+"F4.wireOp",EDGE,"E92.7"),sQuery(id+"F4.wireOp",EDGE,"E92.8"),sQuery(id+"F4.wireOp",EDGE,"E92.9"),sQuery(id+"F4.wireOp",EDGE,"E92.10"),sQuery(id+"F4.wireOp",EDGE,"E92.11"),sQuery(id+"F4.wireOp",EDGE,"E92.12"),sQuery(id+"F4.wireOp",EDGE,"E92.13"),sQuery(id+"F4.wireOp",EDGE,"E92.14"),sQuery(id+"F4.wireOp",EDGE,"E92.15"),sQuery(id+"F4.wireOp",EDGE,"E92.16"),sQuery(id+"F4.wireOp",EDGE,"E92.17"),sQuery(id+"F4.wireOp",EDGE,"E93"),sQuery(id+"F4.wireOp",EDGE,"E94")])],"isStart":false})]});
            var Q11;
            Q11=makeQuery(id+"F6.boolean.opBoolean","INTERSECT",EDGE,{"derivedFrom":[makeQuery(id+"F1.opExtrude","SWEPT_FACE",FACE,{"disambiguationData":[OSD([sQuery(id+"F0.wireOp",EDGE,"E9"),sQuery(id+"F0.wireOp",EDGE,"E60")])]}),makeQuery(id+"F5.opExtrude","CAP_FACE",FACE,{"disambiguationData":[OSD([sQuery(id+"F4.wireOp",EDGE,"E92.0"),sQuery(id+"F4.wireOp",EDGE,"E92.1"),sQuery(id+"F4.wireOp",EDGE,"E92.2"),sQuery(id+"F4.wireOp",EDGE,"E92.3"),sQuery(id+"F4.wireOp",EDGE,"E92.4"),sQuery(id+"F4.wireOp",EDGE,"E92.5"),sQuery(id+"F4.wireOp",EDGE,"E92.6"),sQuery(id+"F4.wireOp",EDGE,"E92.7"),sQuery(id+"F4.wireOp",EDGE,"E92.8"),sQuery(id+"F4.wireOp",EDGE,"E92.9"),sQuery(id+"F4.wireOp",EDGE,"E92.10"),sQuery(id+"F4.wireOp",EDGE,"E92.11"),sQuery(id+"F4.wireOp",EDGE,"E92.12"),sQuery(id+"F4.wireOp",EDGE,"E92.13"),sQuery(id+"F4.wireOp",EDGE,"E92.14"),sQuery(id+"F4.wireOp",EDGE,"E92.15"),sQuery(id+"F4.wireOp",EDGE,"E92.16"),sQuery(id+"F4.wireOp",EDGE,"E92.17"),sQuery(id+"F4.wireOp",EDGE,"E93"),sQuery(id+"F4.wireOp",EDGE,"E94")])],"isStart":false})]});
            var Q12;
            Q12=makeQuery(id+"F6.boolean.opBoolean","INTERSECT",EDGE,{"derivedFrom":[makeQuery(id+"F1.opExtrude","SWEPT_FACE",FACE,{"disambiguationData":[OSD([sQuery(id+"F0.wireOp",EDGE,"E31"),sQuery(id+"F0.wireOp",EDGE,"E85")])]}),makeQuery(id+"F5.opExtrude","CAP_FACE",FACE,{"disambiguationData":[OSD([sQuery(id+"F4.wireOp",EDGE,"E92.0"),sQuery(id+"F4.wireOp",EDGE,"E92.1"),sQuery(id+"F4.wireOp",EDGE,"E92.2"),sQuery(id+"F4.wireOp",EDGE,"E92.3"),sQuery(id+"F4.wireOp",EDGE,"E92.4"),sQuery(id+"F4.wireOp",EDGE,"E92.5"),sQuery(id+"F4.wireOp",EDGE,"E92.6"),sQuery(id+"F4.wireOp",EDGE,"E92.7"),sQuery(id+"F4.wireOp",EDGE,"E92.8"),sQuery(id+"F4.wireOp",EDGE,"E92.9"),sQuery(id+"F4.wireOp",EDGE,"E92.10"),sQuery(id+"F4.wireOp",EDGE,"E92.11"),sQuery(id+"F4.wireOp",EDGE,"E92.12"),sQuery(id+"F4.wireOp",EDGE,"E92.13"),sQuery(id+"F4.wireOp",EDGE,"E92.14"),sQuery(id+"F4.wireOp",EDGE,"E92.15"),sQuery(id+"F4.wireOp",EDGE,"E92.16"),sQuery(id+"F4.wireOp",EDGE,"E92.17"),sQuery(id+"F4.wireOp",EDGE,"E93"),sQuery(id+"F4.wireOp",EDGE,"E94")])],"isStart":false})]});
            var Q13;
            Q13=makeQuery(id+"F6.boolean.opBoolean","INTERSECT",EDGE,{"derivedFrom":[makeQuery(id+"F1.opExtrude","SWEPT_FACE",FACE,{"disambiguationData":[OSD([sQuery(id+"F0.wireOp",EDGE,"E34"),sQuery(id+"F0.wireOp",EDGE,"E89")])]}),makeQuery(id+"F5.opExtrude","CAP_FACE",FACE,{"disambiguationData":[OSD([sQuery(id+"F4.wireOp",EDGE,"E92.0"),sQuery(id+"F4.wireOp",EDGE,"E92.1"),sQuery(id+"F4.wireOp",EDGE,"E92.2"),sQuery(id+"F4.wireOp",EDGE,"E92.3"),sQuery(id+"F4.wireOp",EDGE,"E92.4"),sQuery(id+"F4.wireOp",EDGE,"E92.5"),sQuery(id+"F4.wireOp",EDGE,"E92.6"),sQuery(id+"F4.wireOp",EDGE,"E92.7"),sQuery(id+"F4.wireOp",EDGE,"E92.8"),sQuery(id+"F4.wireOp",EDGE,"E92.9"),sQuery(id+"F4.wireOp",EDGE,"E92.10"),sQuery(id+"F4.wireOp",EDGE,"E92.11"),sQuery(id+"F4.wireOp",EDGE,"E92.12"),sQuery(id+"F4.wireOp",EDGE,"E92.13"),sQuery(id+"F4.wireOp",EDGE,"E92.14"),sQuery(id+"F4.wireOp",EDGE,"E92.15"),sQuery(id+"F4.wireOp",EDGE,"E92.16"),sQuery(id+"F4.wireOp",EDGE,"E92.17"),sQuery(id+"F4.wireOp",EDGE,"E93"),sQuery(id+"F4.wireOp",EDGE,"E94")])],"isStart":false})]});
            var Q14;
            Q14=makeQuery(id+"F6.boolean.opBoolean","INTERSECT",EDGE,{"derivedFrom":[makeQuery(id+"F1.opExtrude","SWEPT_FACE",FACE,{"disambiguationData":[OSD([sQuery(id+"F0.wireOp",EDGE,"E36"),sQuery(id+"F0.wireOp",EDGE,"E87")])]}),makeQuery(id+"F5.opExtrude","CAP_FACE",FACE,{"disambiguationData":[OSD([sQuery(id+"F4.wireOp",EDGE,"E92.0"),sQuery(id+"F4.wireOp",EDGE,"E92.1"),sQuery(id+"F4.wireOp",EDGE,"E92.2"),sQuery(id+"F4.wireOp",EDGE,"E92.3"),sQuery(id+"F4.wireOp",EDGE,"E92.4"),sQuery(id+"F4.wireOp",EDGE,"E92.5"),sQuery(id+"F4.wireOp",EDGE,"E92.6"),sQuery(id+"F4.wireOp",EDGE,"E92.7"),sQuery(id+"F4.wireOp",EDGE,"E92.8"),sQuery(id+"F4.wireOp",EDGE,"E92.9"),sQuery(id+"F4.wireOp",EDGE,"E92.10"),sQuery(id+"F4.wireOp",EDGE,"E92.11"),sQuery(id+"F4.wireOp",EDGE,"E92.12"),sQuery(id+"F4.wireOp",EDGE,"E92.13"),sQuery(id+"F4.wireOp",EDGE,"E92.14"),sQuery(id+"F4.wireOp",EDGE,"E92.15"),sQuery(id+"F4.wireOp",EDGE,"E92.16"),sQuery(id+"F4.wireOp",EDGE,"E92.17"),sQuery(id+"F4.wireOp",EDGE,"E93"),sQuery(id+"F4.wireOp",EDGE,"E94")])],"isStart":false})]});
            var Q15;
            Q15=makeQuery(id+"F6.boolean.opBoolean","INTERSECT",EDGE,{"derivedFrom":[makeQuery(id+"F1.opExtrude","SWEPT_FACE",FACE,{"disambiguationData":[OSD([sQuery(id+"F0.wireOp",EDGE,"E38"),sQuery(id+"F0.wireOp",EDGE,"E67")])]}),makeQuery(id+"F5.opExtrude","CAP_FACE",FACE,{"disambiguationData":[OSD([sQuery(id+"F4.wireOp",EDGE,"E92.0"),sQuery(id+"F4.wireOp",EDGE,"E92.1"),sQuery(id+"F4.wireOp",EDGE,"E92.2"),sQuery(id+"F4.wireOp",EDGE,"E92.3"),sQuery(id+"F4.wireOp",EDGE,"E92.4"),sQuery(id+"F4.wireOp",EDGE,"E92.5"),sQuery(id+"F4.wireOp",EDGE,"E92.6"),sQuery(id+"F4.wireOp",EDGE,"E92.7"),sQuery(id+"F4.wireOp",EDGE,"E92.8"),sQuery(id+"F4.wireOp",EDGE,"E92.9"),sQuery(id+"F4.wireOp",EDGE,"E92.10"),sQuery(id+"F4.wireOp",EDGE,"E92.11"),sQuery(id+"F4.wireOp",EDGE,"E92.12"),sQuery(id+"F4.wireOp",EDGE,"E92.13"),sQuery(id+"F4.wireOp",EDGE,"E92.14"),sQuery(id+"F4.wireOp",EDGE,"E92.15"),sQuery(id+"F4.wireOp",EDGE,"E92.16"),sQuery(id+"F4.wireOp",EDGE,"E92.17"),sQuery(id+"F4.wireOp",EDGE,"E93"),sQuery(id+"F4.wireOp",EDGE,"E94")])],"isStart":false})]});
            var Q16;
            Q16=makeQuery(id+"F6.boolean.opBoolean","INTERSECT",EDGE,{"derivedFrom":[makeQuery(id+"F1.opExtrude","SWEPT_FACE",FACE,{"disambiguationData":[OSD([sQuery(id+"F0.wireOp",EDGE,"E42"),sQuery(id+"F0.wireOp",EDGE,"E74")])]}),makeQuery(id+"F5.opExtrude","CAP_FACE",FACE,{"disambiguationData":[OSD([sQuery(id+"F4.wireOp",EDGE,"E92.0"),sQuery(id+"F4.wireOp",EDGE,"E92.1"),sQuery(id+"F4.wireOp",EDGE,"E92.2"),sQuery(id+"F4.wireOp",EDGE,"E92.3"),sQuery(id+"F4.wireOp",EDGE,"E92.4"),sQuery(id+"F4.wireOp",EDGE,"E92.5"),sQuery(id+"F4.wireOp",EDGE,"E92.6"),sQuery(id+"F4.wireOp",EDGE,"E92.7"),sQuery(id+"F4.wireOp",EDGE,"E92.8"),sQuery(id+"F4.wireOp",EDGE,"E92.9"),sQuery(id+"F4.wireOp",EDGE,"E92.10"),sQuery(id+"F4.wireOp",EDGE,"E92.11"),sQuery(id+"F4.wireOp",EDGE,"E92.12"),sQuery(id+"F4.wireOp",EDGE,"E92.13"),sQuery(id+"F4.wireOp",EDGE,"E92.14"),sQuery(id+"F4.wireOp",EDGE,"E92.15"),sQuery(id+"F4.wireOp",EDGE,"E92.16"),sQuery(id+"F4.wireOp",EDGE,"E92.17"),sQuery(id+"F4.wireOp",EDGE,"E93"),sQuery(id+"F4.wireOp",EDGE,"E94")])],"isStart":false})]});
            var Q17;
            Q17=makeQuery(id+"F6.boolean.opBoolean","INTERSECT",EDGE,{"derivedFrom":[makeQuery(id+"F1.opExtrude","SWEPT_FACE",FACE,{"disambiguationData":[OSD([sQuery(id+"F0.wireOp",EDGE,"E4"),sQuery(id+"F0.wireOp",EDGE,"E70")])]}),makeQuery(id+"F5.opExtrude","CAP_FACE",FACE,{"disambiguationData":[OSD([sQuery(id+"F4.wireOp",EDGE,"E92.0"),sQuery(id+"F4.wireOp",EDGE,"E92.1"),sQuery(id+"F4.wireOp",EDGE,"E92.2"),sQuery(id+"F4.wireOp",EDGE,"E92.3"),sQuery(id+"F4.wireOp",EDGE,"E92.4"),sQuery(id+"F4.wireOp",EDGE,"E92.5"),sQuery(id+"F4.wireOp",EDGE,"E92.6"),sQuery(id+"F4.wireOp",EDGE,"E92.7"),sQuery(id+"F4.wireOp",EDGE,"E92.8"),sQuery(id+"F4.wireOp",EDGE,"E92.9"),sQuery(id+"F4.wireOp",EDGE,"E92.10"),sQuery(id+"F4.wireOp",EDGE,"E92.11"),sQuery(id+"F4.wireOp",EDGE,"E92.12"),sQuery(id+"F4.wireOp",EDGE,"E92.13"),sQuery(id+"F4.wireOp",EDGE,"E92.14"),sQuery(id+"F4.wireOp",EDGE,"E92.15"),sQuery(id+"F4.wireOp",EDGE,"E92.16"),sQuery(id+"F4.wireOp",EDGE,"E92.17"),sQuery(id+"F4.wireOp",EDGE,"E93"),sQuery(id+"F4.wireOp",EDGE,"E94")])],"isStart":false})]});
            var Q18;
            Q18=makeQuery(id+"F6.boolean.opBoolean","INTERSECT",EDGE,{"derivedFrom":[makeQuery(id+"F1.opExtrude","SWEPT_FACE",FACE,{"disambiguationData":[OSD([sQuery(id+"F0.wireOp",EDGE,"E44"),sQuery(id+"F0.wireOp",EDGE,"E90")])]}),makeQuery(id+"F5.opExtrude","CAP_FACE",FACE,{"disambiguationData":[OSD([sQuery(id+"F4.wireOp",EDGE,"E92.0"),sQuery(id+"F4.wireOp",EDGE,"E92.1"),sQuery(id+"F4.wireOp",EDGE,"E92.2"),sQuery(id+"F4.wireOp",EDGE,"E92.3"),sQuery(id+"F4.wireOp",EDGE,"E92.4"),sQuery(id+"F4.wireOp",EDGE,"E92.5"),sQuery(id+"F4.wireOp",EDGE,"E92.6"),sQuery(id+"F4.wireOp",EDGE,"E92.7"),sQuery(id+"F4.wireOp",EDGE,"E92.8"),sQuery(id+"F4.wireOp",EDGE,"E92.9"),sQuery(id+"F4.wireOp",EDGE,"E92.10"),sQuery(id+"F4.wireOp",EDGE,"E92.11"),sQuery(id+"F4.wireOp",EDGE,"E92.12"),sQuery(id+"F4.wireOp",EDGE,"E92.13"),sQuery(id+"F4.wireOp",EDGE,"E92.14"),sQuery(id+"F4.wireOp",EDGE,"E92.15"),sQuery(id+"F4.wireOp",EDGE,"E92.16"),sQuery(id+"F4.wireOp",EDGE,"E92.17"),sQuery(id+"F4.wireOp",EDGE,"E93"),sQuery(id+"F4.wireOp",EDGE,"E94")])],"isStart":false})]});
            var Q19;
            Q19=makeQuery(id+"F6.boolean.opBoolean","INTERSECT",EDGE,{"derivedFrom":[makeQuery(id+"F1.opExtrude","SWEPT_FACE",FACE,{"disambiguationData":[OSD([sQuery(id+"F0.wireOp",EDGE,"E44"),sQuery(id+"F0.wireOp",EDGE,"E90")])]}),makeQuery(id+"F6.opPattern","COPY",FACE,{"derivedFrom":makeQuery(id+"F5.opExtrude","CAP_FACE",FACE,{"disambiguationData":[OSD([sQuery(id+"F4.wireOp",EDGE,"E92.0"),sQuery(id+"F4.wireOp",EDGE,"E92.1"),sQuery(id+"F4.wireOp",EDGE,"E92.2"),sQuery(id+"F4.wireOp",EDGE,"E92.3"),sQuery(id+"F4.wireOp",EDGE,"E92.4"),sQuery(id+"F4.wireOp",EDGE,"E92.5"),sQuery(id+"F4.wireOp",EDGE,"E92.6"),sQuery(id+"F4.wireOp",EDGE,"E92.7"),sQuery(id+"F4.wireOp",EDGE,"E92.8"),sQuery(id+"F4.wireOp",EDGE,"E92.9"),sQuery(id+"F4.wireOp",EDGE,"E92.10"),sQuery(id+"F4.wireOp",EDGE,"E92.11"),sQuery(id+"F4.wireOp",EDGE,"E92.12"),sQuery(id+"F4.wireOp",EDGE,"E92.13"),sQuery(id+"F4.wireOp",EDGE,"E92.14"),sQuery(id+"F4.wireOp",EDGE,"E92.15"),sQuery(id+"F4.wireOp",EDGE,"E92.16"),sQuery(id+"F4.wireOp",EDGE,"E92.17"),sQuery(id+"F4.wireOp",EDGE,"E93"),sQuery(id+"F4.wireOp",EDGE,"E94")])],"isStart":false}),"instanceName":"1"})]});
            var Q20;
            Q20=makeQuery(id+"F6.boolean.opBoolean","INTERSECT",EDGE,{"derivedFrom":[makeQuery(id+"F1.opExtrude","SWEPT_FACE",FACE,{"disambiguationData":[OSD([sQuery(id+"F0.wireOp",EDGE,"E40"),sQuery(id+"F0.wireOp",EDGE,"E69")])]}),makeQuery(id+"F6.opPattern","COPY",FACE,{"derivedFrom":makeQuery(id+"F5.opExtrude","CAP_FACE",FACE,{"disambiguationData":[OSD([sQuery(id+"F4.wireOp",EDGE,"E92.0"),sQuery(id+"F4.wireOp",EDGE,"E92.1"),sQuery(id+"F4.wireOp",EDGE,"E92.2"),sQuery(id+"F4.wireOp",EDGE,"E92.3"),sQuery(id+"F4.wireOp",EDGE,"E92.4"),sQuery(id+"F4.wireOp",EDGE,"E92.5"),sQuery(id+"F4.wireOp",EDGE,"E92.6"),sQuery(id+"F4.wireOp",EDGE,"E92.7"),sQuery(id+"F4.wireOp",EDGE,"E92.8"),sQuery(id+"F4.wireOp",EDGE,"E92.9"),sQuery(id+"F4.wireOp",EDGE,"E92.10"),sQuery(id+"F4.wireOp",EDGE,"E92.11"),sQuery(id+"F4.wireOp",EDGE,"E92.12"),sQuery(id+"F4.wireOp",EDGE,"E92.13"),sQuery(id+"F4.wireOp",EDGE,"E92.14"),sQuery(id+"F4.wireOp",EDGE,"E92.15"),sQuery(id+"F4.wireOp",EDGE,"E92.16"),sQuery(id+"F4.wireOp",EDGE,"E92.17"),sQuery(id+"F4.wireOp",EDGE,"E93"),sQuery(id+"F4.wireOp",EDGE,"E94")])],"isStart":false}),"instanceName":"1"})]});
            var Q21;
            Q21=makeQuery(id+"F6.boolean.opBoolean","INTERSECT",EDGE,{"derivedFrom":[makeQuery(id+"F1.opExtrude","SWEPT_FACE",FACE,{"disambiguationData":[OSD([sQuery(id+"F0.wireOp",EDGE,"E36"),sQuery(id+"F0.wireOp",EDGE,"E87")])]}),makeQuery(id+"F6.opPattern","COPY",FACE,{"derivedFrom":makeQuery(id+"F5.opExtrude","CAP_FACE",FACE,{"disambiguationData":[OSD([sQuery(id+"F4.wireOp",EDGE,"E92.0"),sQuery(id+"F4.wireOp",EDGE,"E92.1"),sQuery(id+"F4.wireOp",EDGE,"E92.2"),sQuery(id+"F4.wireOp",EDGE,"E92.3"),sQuery(id+"F4.wireOp",EDGE,"E92.4"),sQuery(id+"F4.wireOp",EDGE,"E92.5"),sQuery(id+"F4.wireOp",EDGE,"E92.6"),sQuery(id+"F4.wireOp",EDGE,"E92.7"),sQuery(id+"F4.wireOp",EDGE,"E92.8"),sQuery(id+"F4.wireOp",EDGE,"E92.9"),sQuery(id+"F4.wireOp",EDGE,"E92.10"),sQuery(id+"F4.wireOp",EDGE,"E92.11"),sQuery(id+"F4.wireOp",EDGE,"E92.12"),sQuery(id+"F4.wireOp",EDGE,"E92.13"),sQuery(id+"F4.wireOp",EDGE,"E92.14"),sQuery(id+"F4.wireOp",EDGE,"E92.15"),sQuery(id+"F4.wireOp",EDGE,"E92.16"),sQuery(id+"F4.wireOp",EDGE,"E92.17"),sQuery(id+"F4.wireOp",EDGE,"E93"),sQuery(id+"F4.wireOp",EDGE,"E94")])],"isStart":false}),"instanceName":"1"})]});
            var Q22;
            Q22=makeQuery(id+"F6.boolean.opBoolean","INTERSECT",EDGE,{"derivedFrom":[makeQuery(id+"F1.opExtrude","SWEPT_FACE",FACE,{"disambiguationData":[OSD([sQuery(id+"F0.wireOp",EDGE,"E31"),sQuery(id+"F0.wireOp",EDGE,"E85")])]}),makeQuery(id+"F6.opPattern","COPY",FACE,{"derivedFrom":makeQuery(id+"F5.opExtrude","CAP_FACE",FACE,{"disambiguationData":[OSD([sQuery(id+"F4.wireOp",EDGE,"E92.0"),sQuery(id+"F4.wireOp",EDGE,"E92.1"),sQuery(id+"F4.wireOp",EDGE,"E92.2"),sQuery(id+"F4.wireOp",EDGE,"E92.3"),sQuery(id+"F4.wireOp",EDGE,"E92.4"),sQuery(id+"F4.wireOp",EDGE,"E92.5"),sQuery(id+"F4.wireOp",EDGE,"E92.6"),sQuery(id+"F4.wireOp",EDGE,"E92.7"),sQuery(id+"F4.wireOp",EDGE,"E92.8"),sQuery(id+"F4.wireOp",EDGE,"E92.9"),sQuery(id+"F4.wireOp",EDGE,"E92.10"),sQuery(id+"F4.wireOp",EDGE,"E92.11"),sQuery(id+"F4.wireOp",EDGE,"E92.12"),sQuery(id+"F4.wireOp",EDGE,"E92.13"),sQuery(id+"F4.wireOp",EDGE,"E92.14"),sQuery(id+"F4.wireOp",EDGE,"E92.15"),sQuery(id+"F4.wireOp",EDGE,"E92.16"),sQuery(id+"F4.wireOp",EDGE,"E92.17"),sQuery(id+"F4.wireOp",EDGE,"E93"),sQuery(id+"F4.wireOp",EDGE,"E94")])],"isStart":false}),"instanceName":"1"})]});
            var Q23;
            Q23=makeQuery(id+"F6.boolean.opBoolean","INTERSECT",EDGE,{"derivedFrom":[makeQuery(id+"F1.opExtrude","SWEPT_FACE",FACE,{"disambiguationData":[OSD([sQuery(id+"F0.wireOp",EDGE,"E27"),sQuery(id+"F0.wireOp",EDGE,"E83")])]}),makeQuery(id+"F6.opPattern","COPY",FACE,{"derivedFrom":makeQuery(id+"F5.opExtrude","CAP_FACE",FACE,{"disambiguationData":[OSD([sQuery(id+"F4.wireOp",EDGE,"E92.0"),sQuery(id+"F4.wireOp",EDGE,"E92.1"),sQuery(id+"F4.wireOp",EDGE,"E92.2"),sQuery(id+"F4.wireOp",EDGE,"E92.3"),sQuery(id+"F4.wireOp",EDGE,"E92.4"),sQuery(id+"F4.wireOp",EDGE,"E92.5"),sQuery(id+"F4.wireOp",EDGE,"E92.6"),sQuery(id+"F4.wireOp",EDGE,"E92.7"),sQuery(id+"F4.wireOp",EDGE,"E92.8"),sQuery(id+"F4.wireOp",EDGE,"E92.9"),sQuery(id+"F4.wireOp",EDGE,"E92.10"),sQuery(id+"F4.wireOp",EDGE,"E92.11"),sQuery(id+"F4.wireOp",EDGE,"E92.12"),sQuery(id+"F4.wireOp",EDGE,"E92.13"),sQuery(id+"F4.wireOp",EDGE,"E92.14"),sQuery(id+"F4.wireOp",EDGE,"E92.15"),sQuery(id+"F4.wireOp",EDGE,"E92.16"),sQuery(id+"F4.wireOp",EDGE,"E92.17"),sQuery(id+"F4.wireOp",EDGE,"E93"),sQuery(id+"F4.wireOp",EDGE,"E94")])],"isStart":false}),"instanceName":"1"})]});
            var Q24;
            Q24=makeQuery(id+"F6.boolean.opBoolean","INTERSECT",EDGE,{"derivedFrom":[makeQuery(id+"F1.opExtrude","SWEPT_FACE",FACE,{"disambiguationData":[OSD([sQuery(id+"F0.wireOp",EDGE,"E22"),sQuery(id+"F0.wireOp",EDGE,"E82")])]}),makeQuery(id+"F6.opPattern","COPY",FACE,{"derivedFrom":makeQuery(id+"F5.opExtrude","CAP_FACE",FACE,{"disambiguationData":[OSD([sQuery(id+"F4.wireOp",EDGE,"E92.0"),sQuery(id+"F4.wireOp",EDGE,"E92.1"),sQuery(id+"F4.wireOp",EDGE,"E92.2"),sQuery(id+"F4.wireOp",EDGE,"E92.3"),sQuery(id+"F4.wireOp",EDGE,"E92.4"),sQuery(id+"F4.wireOp",EDGE,"E92.5"),sQuery(id+"F4.wireOp",EDGE,"E92.6"),sQuery(id+"F4.wireOp",EDGE,"E92.7"),sQuery(id+"F4.wireOp",EDGE,"E92.8"),sQuery(id+"F4.wireOp",EDGE,"E92.9"),sQuery(id+"F4.wireOp",EDGE,"E92.10"),sQuery(id+"F4.wireOp",EDGE,"E92.11"),sQuery(id+"F4.wireOp",EDGE,"E92.12"),sQuery(id+"F4.wireOp",EDGE,"E92.13"),sQuery(id+"F4.wireOp",EDGE,"E92.14"),sQuery(id+"F4.wireOp",EDGE,"E92.15"),sQuery(id+"F4.wireOp",EDGE,"E92.16"),sQuery(id+"F4.wireOp",EDGE,"E92.17"),sQuery(id+"F4.wireOp",EDGE,"E93"),sQuery(id+"F4.wireOp",EDGE,"E94")])],"isStart":false}),"instanceName":"1"})]});
            var Q25;
            Q25=makeQuery(id+"F6.boolean.opBoolean","INTERSECT",EDGE,{"derivedFrom":[makeQuery(id+"F1.opExtrude","SWEPT_FACE",FACE,{"disambiguationData":[OSD([sQuery(id+"F0.wireOp",EDGE,"E18"),sQuery(id+"F0.wireOp",EDGE,"E78")])]}),makeQuery(id+"F6.opPattern","COPY",FACE,{"derivedFrom":makeQuery(id+"F5.opExtrude","CAP_FACE",FACE,{"disambiguationData":[OSD([sQuery(id+"F4.wireOp",EDGE,"E92.0"),sQuery(id+"F4.wireOp",EDGE,"E92.1"),sQuery(id+"F4.wireOp",EDGE,"E92.2"),sQuery(id+"F4.wireOp",EDGE,"E92.3"),sQuery(id+"F4.wireOp",EDGE,"E92.4"),sQuery(id+"F4.wireOp",EDGE,"E92.5"),sQuery(id+"F4.wireOp",EDGE,"E92.6"),sQuery(id+"F4.wireOp",EDGE,"E92.7"),sQuery(id+"F4.wireOp",EDGE,"E92.8"),sQuery(id+"F4.wireOp",EDGE,"E92.9"),sQuery(id+"F4.wireOp",EDGE,"E92.10"),sQuery(id+"F4.wireOp",EDGE,"E92.11"),sQuery(id+"F4.wireOp",EDGE,"E92.12"),sQuery(id+"F4.wireOp",EDGE,"E92.13"),sQuery(id+"F4.wireOp",EDGE,"E92.14"),sQuery(id+"F4.wireOp",EDGE,"E92.15"),sQuery(id+"F4.wireOp",EDGE,"E92.16"),sQuery(id+"F4.wireOp",EDGE,"E92.17"),sQuery(id+"F4.wireOp",EDGE,"E93"),sQuery(id+"F4.wireOp",EDGE,"E94")])],"isStart":false}),"instanceName":"1"})]});
            var Q26;
            Q26=makeQuery(id+"F6.boolean.opBoolean","INTERSECT",EDGE,{"derivedFrom":[makeQuery(id+"F1.opExtrude","SWEPT_FACE",FACE,{"disambiguationData":[OSD([sQuery(id+"F0.wireOp",EDGE,"E15"),sQuery(id+"F0.wireOp",EDGE,"E65")])]}),makeQuery(id+"F6.opPattern","COPY",FACE,{"derivedFrom":makeQuery(id+"F5.opExtrude","CAP_FACE",FACE,{"disambiguationData":[OSD([sQuery(id+"F4.wireOp",EDGE,"E92.0"),sQuery(id+"F4.wireOp",EDGE,"E92.1"),sQuery(id+"F4.wireOp",EDGE,"E92.2"),sQuery(id+"F4.wireOp",EDGE,"E92.3"),sQuery(id+"F4.wireOp",EDGE,"E92.4"),sQuery(id+"F4.wireOp",EDGE,"E92.5"),sQuery(id+"F4.wireOp",EDGE,"E92.6"),sQuery(id+"F4.wireOp",EDGE,"E92.7"),sQuery(id+"F4.wireOp",EDGE,"E92.8"),sQuery(id+"F4.wireOp",EDGE,"E92.9"),sQuery(id+"F4.wireOp",EDGE,"E92.10"),sQuery(id+"F4.wireOp",EDGE,"E92.11"),sQuery(id+"F4.wireOp",EDGE,"E92.12"),sQuery(id+"F4.wireOp",EDGE,"E92.13"),sQuery(id+"F4.wireOp",EDGE,"E92.14"),sQuery(id+"F4.wireOp",EDGE,"E92.15"),sQuery(id+"F4.wireOp",EDGE,"E92.16"),sQuery(id+"F4.wireOp",EDGE,"E92.17"),sQuery(id+"F4.wireOp",EDGE,"E93"),sQuery(id+"F4.wireOp",EDGE,"E94")])],"isStart":false}),"instanceName":"1"})]});
            var Q27;
            Q27=makeQuery(id+"F6.boolean.opBoolean","INTERSECT",EDGE,{"derivedFrom":[makeQuery(id+"F1.opExtrude","SWEPT_FACE",FACE,{"disambiguationData":[OSD([sQuery(id+"F0.wireOp",EDGE,"E11"),sQuery(id+"F0.wireOp",EDGE,"E62")])]}),makeQuery(id+"F6.opPattern","COPY",FACE,{"derivedFrom":makeQuery(id+"F5.opExtrude","CAP_FACE",FACE,{"disambiguationData":[OSD([sQuery(id+"F4.wireOp",EDGE,"E92.0"),sQuery(id+"F4.wireOp",EDGE,"E92.1"),sQuery(id+"F4.wireOp",EDGE,"E92.2"),sQuery(id+"F4.wireOp",EDGE,"E92.3"),sQuery(id+"F4.wireOp",EDGE,"E92.4"),sQuery(id+"F4.wireOp",EDGE,"E92.5"),sQuery(id+"F4.wireOp",EDGE,"E92.6"),sQuery(id+"F4.wireOp",EDGE,"E92.7"),sQuery(id+"F4.wireOp",EDGE,"E92.8"),sQuery(id+"F4.wireOp",EDGE,"E92.9"),sQuery(id+"F4.wireOp",EDGE,"E92.10"),sQuery(id+"F4.wireOp",EDGE,"E92.11"),sQuery(id+"F4.wireOp",EDGE,"E92.12"),sQuery(id+"F4.wireOp",EDGE,"E92.13"),sQuery(id+"F4.wireOp",EDGE,"E92.14"),sQuery(id+"F4.wireOp",EDGE,"E92.15"),sQuery(id+"F4.wireOp",EDGE,"E92.16"),sQuery(id+"F4.wireOp",EDGE,"E92.17"),sQuery(id+"F4.wireOp",EDGE,"E93"),sQuery(id+"F4.wireOp",EDGE,"E94")])],"isStart":false}),"instanceName":"1"})]});
            var Q28;
            Q28=makeQuery(id+"F6.boolean.opBoolean","INTERSECT",EDGE,{"derivedFrom":[makeQuery(id+"F1.opExtrude","SWEPT_FACE",FACE,{"disambiguationData":[OSD([sQuery(id+"F0.wireOp",EDGE,"E7"),sQuery(id+"F0.wireOp",EDGE,"E59")])]}),makeQuery(id+"F6.opPattern","COPY",FACE,{"derivedFrom":makeQuery(id+"F5.opExtrude","CAP_FACE",FACE,{"disambiguationData":[OSD([sQuery(id+"F4.wireOp",EDGE,"E92.0"),sQuery(id+"F4.wireOp",EDGE,"E92.1"),sQuery(id+"F4.wireOp",EDGE,"E92.2"),sQuery(id+"F4.wireOp",EDGE,"E92.3"),sQuery(id+"F4.wireOp",EDGE,"E92.4"),sQuery(id+"F4.wireOp",EDGE,"E92.5"),sQuery(id+"F4.wireOp",EDGE,"E92.6"),sQuery(id+"F4.wireOp",EDGE,"E92.7"),sQuery(id+"F4.wireOp",EDGE,"E92.8"),sQuery(id+"F4.wireOp",EDGE,"E92.9"),sQuery(id+"F4.wireOp",EDGE,"E92.10"),sQuery(id+"F4.wireOp",EDGE,"E92.11"),sQuery(id+"F4.wireOp",EDGE,"E92.12"),sQuery(id+"F4.wireOp",EDGE,"E92.13"),sQuery(id+"F4.wireOp",EDGE,"E92.14"),sQuery(id+"F4.wireOp",EDGE,"E92.15"),sQuery(id+"F4.wireOp",EDGE,"E92.16"),sQuery(id+"F4.wireOp",EDGE,"E92.17"),sQuery(id+"F4.wireOp",EDGE,"E93"),sQuery(id+"F4.wireOp",EDGE,"E94")])],"isStart":false}),"instanceName":"1"})]});
            var Q29;
            Q29=makeQuery(id+"F6.boolean.opBoolean","INTERSECT",EDGE,{"derivedFrom":[makeQuery(id+"F1.opExtrude","SWEPT_FACE",FACE,{"disambiguationData":[OSD([sQuery(id+"F0.wireOp",EDGE,"E4"),sQuery(id+"F0.wireOp",EDGE,"E70")])]}),makeQuery(id+"F6.opPattern","COPY",FACE,{"derivedFrom":makeQuery(id+"F5.opExtrude","CAP_FACE",FACE,{"disambiguationData":[OSD([sQuery(id+"F4.wireOp",EDGE,"E92.0"),sQuery(id+"F4.wireOp",EDGE,"E92.1"),sQuery(id+"F4.wireOp",EDGE,"E92.2"),sQuery(id+"F4.wireOp",EDGE,"E92.3"),sQuery(id+"F4.wireOp",EDGE,"E92.4"),sQuery(id+"F4.wireOp",EDGE,"E92.5"),sQuery(id+"F4.wireOp",EDGE,"E92.6"),sQuery(id+"F4.wireOp",EDGE,"E92.7"),sQuery(id+"F4.wireOp",EDGE,"E92.8"),sQuery(id+"F4.wireOp",EDGE,"E92.9"),sQuery(id+"F4.wireOp",EDGE,"E92.10"),sQuery(id+"F4.wireOp",EDGE,"E92.11"),sQuery(id+"F4.wireOp",EDGE,"E92.12"),sQuery(id+"F4.wireOp",EDGE,"E92.13"),sQuery(id+"F4.wireOp",EDGE,"E92.14"),sQuery(id+"F4.wireOp",EDGE,"E92.15"),sQuery(id+"F4.wireOp",EDGE,"E92.16"),sQuery(id+"F4.wireOp",EDGE,"E92.17"),sQuery(id+"F4.wireOp",EDGE,"E93"),sQuery(id+"F4.wireOp",EDGE,"E94")])],"isStart":false}),"instanceName":"1"})]});
            var Q30;
            Q30=makeQuery(id+"F6.boolean.opBoolean","INTERSECT",EDGE,{"derivedFrom":[makeQuery(id+"F1.opExtrude","SWEPT_FACE",FACE,{"disambiguationData":[OSD([sQuery(id+"F0.wireOp",EDGE,"E42"),sQuery(id+"F0.wireOp",EDGE,"E74")])]}),makeQuery(id+"F6.opPattern","COPY",FACE,{"derivedFrom":makeQuery(id+"F5.opExtrude","CAP_FACE",FACE,{"disambiguationData":[OSD([sQuery(id+"F4.wireOp",EDGE,"E92.0"),sQuery(id+"F4.wireOp",EDGE,"E92.1"),sQuery(id+"F4.wireOp",EDGE,"E92.2"),sQuery(id+"F4.wireOp",EDGE,"E92.3"),sQuery(id+"F4.wireOp",EDGE,"E92.4"),sQuery(id+"F4.wireOp",EDGE,"E92.5"),sQuery(id+"F4.wireOp",EDGE,"E92.6"),sQuery(id+"F4.wireOp",EDGE,"E92.7"),sQuery(id+"F4.wireOp",EDGE,"E92.8"),sQuery(id+"F4.wireOp",EDGE,"E92.9"),sQuery(id+"F4.wireOp",EDGE,"E92.10"),sQuery(id+"F4.wireOp",EDGE,"E92.11"),sQuery(id+"F4.wireOp",EDGE,"E92.12"),sQuery(id+"F4.wireOp",EDGE,"E92.13"),sQuery(id+"F4.wireOp",EDGE,"E92.14"),sQuery(id+"F4.wireOp",EDGE,"E92.15"),sQuery(id+"F4.wireOp",EDGE,"E92.16"),sQuery(id+"F4.wireOp",EDGE,"E92.17"),sQuery(id+"F4.wireOp",EDGE,"E93"),sQuery(id+"F4.wireOp",EDGE,"E94")])],"isStart":false}),"instanceName":"1"})]});
            var Q31;
            Q31=makeQuery(id+"F6.boolean.opBoolean","INTERSECT",EDGE,{"derivedFrom":[makeQuery(id+"F1.opExtrude","SWEPT_FACE",FACE,{"disambiguationData":[OSD([sQuery(id+"F0.wireOp",EDGE,"E38"),sQuery(id+"F0.wireOp",EDGE,"E67")])]}),makeQuery(id+"F6.opPattern","COPY",FACE,{"derivedFrom":makeQuery(id+"F5.opExtrude","CAP_FACE",FACE,{"disambiguationData":[OSD([sQuery(id+"F4.wireOp",EDGE,"E92.0"),sQuery(id+"F4.wireOp",EDGE,"E92.1"),sQuery(id+"F4.wireOp",EDGE,"E92.2"),sQuery(id+"F4.wireOp",EDGE,"E92.3"),sQuery(id+"F4.wireOp",EDGE,"E92.4"),sQuery(id+"F4.wireOp",EDGE,"E92.5"),sQuery(id+"F4.wireOp",EDGE,"E92.6"),sQuery(id+"F4.wireOp",EDGE,"E92.7"),sQuery(id+"F4.wireOp",EDGE,"E92.8"),sQuery(id+"F4.wireOp",EDGE,"E92.9"),sQuery(id+"F4.wireOp",EDGE,"E92.10"),sQuery(id+"F4.wireOp",EDGE,"E92.11"),sQuery(id+"F4.wireOp",EDGE,"E92.12"),sQuery(id+"F4.wireOp",EDGE,"E92.13"),sQuery(id+"F4.wireOp",EDGE,"E92.14"),sQuery(id+"F4.wireOp",EDGE,"E92.15"),sQuery(id+"F4.wireOp",EDGE,"E92.16"),sQuery(id+"F4.wireOp",EDGE,"E92.17"),sQuery(id+"F4.wireOp",EDGE,"E93"),sQuery(id+"F4.wireOp",EDGE,"E94")])],"isStart":false}),"instanceName":"1"})]});
            var Q32;
            Q32=makeQuery(id+"F6.boolean.opBoolean","INTERSECT",EDGE,{"derivedFrom":[makeQuery(id+"F1.opExtrude","SWEPT_FACE",FACE,{"disambiguationData":[OSD([sQuery(id+"F0.wireOp",EDGE,"E34"),sQuery(id+"F0.wireOp",EDGE,"E89")])]}),makeQuery(id+"F6.opPattern","COPY",FACE,{"derivedFrom":makeQuery(id+"F5.opExtrude","CAP_FACE",FACE,{"disambiguationData":[OSD([sQuery(id+"F4.wireOp",EDGE,"E92.0"),sQuery(id+"F4.wireOp",EDGE,"E92.1"),sQuery(id+"F4.wireOp",EDGE,"E92.2"),sQuery(id+"F4.wireOp",EDGE,"E92.3"),sQuery(id+"F4.wireOp",EDGE,"E92.4"),sQuery(id+"F4.wireOp",EDGE,"E92.5"),sQuery(id+"F4.wireOp",EDGE,"E92.6"),sQuery(id+"F4.wireOp",EDGE,"E92.7"),sQuery(id+"F4.wireOp",EDGE,"E92.8"),sQuery(id+"F4.wireOp",EDGE,"E92.9"),sQuery(id+"F4.wireOp",EDGE,"E92.10"),sQuery(id+"F4.wireOp",EDGE,"E92.11"),sQuery(id+"F4.wireOp",EDGE,"E92.12"),sQuery(id+"F4.wireOp",EDGE,"E92.13"),sQuery(id+"F4.wireOp",EDGE,"E92.14"),sQuery(id+"F4.wireOp",EDGE,"E92.15"),sQuery(id+"F4.wireOp",EDGE,"E92.16"),sQuery(id+"F4.wireOp",EDGE,"E92.17"),sQuery(id+"F4.wireOp",EDGE,"E93"),sQuery(id+"F4.wireOp",EDGE,"E94")])],"isStart":false}),"instanceName":"1"})]});
            var Q33;
            Q33=makeQuery(id+"F6.boolean.opBoolean","INTERSECT",EDGE,{"derivedFrom":[makeQuery(id+"F1.opExtrude","SWEPT_FACE",FACE,{"disambiguationData":[OSD([sQuery(id+"F0.wireOp",EDGE,"E29"),sQuery(id+"F0.wireOp",EDGE,"E75")])]}),makeQuery(id+"F6.opPattern","COPY",FACE,{"derivedFrom":makeQuery(id+"F5.opExtrude","CAP_FACE",FACE,{"disambiguationData":[OSD([sQuery(id+"F4.wireOp",EDGE,"E92.0"),sQuery(id+"F4.wireOp",EDGE,"E92.1"),sQuery(id+"F4.wireOp",EDGE,"E92.2"),sQuery(id+"F4.wireOp",EDGE,"E92.3"),sQuery(id+"F4.wireOp",EDGE,"E92.4"),sQuery(id+"F4.wireOp",EDGE,"E92.5"),sQuery(id+"F4.wireOp",EDGE,"E92.6"),sQuery(id+"F4.wireOp",EDGE,"E92.7"),sQuery(id+"F4.wireOp",EDGE,"E92.8"),sQuery(id+"F4.wireOp",EDGE,"E92.9"),sQuery(id+"F4.wireOp",EDGE,"E92.10"),sQuery(id+"F4.wireOp",EDGE,"E92.11"),sQuery(id+"F4.wireOp",EDGE,"E92.12"),sQuery(id+"F4.wireOp",EDGE,"E92.13"),sQuery(id+"F4.wireOp",EDGE,"E92.14"),sQuery(id+"F4.wireOp",EDGE,"E92.15"),sQuery(id+"F4.wireOp",EDGE,"E92.16"),sQuery(id+"F4.wireOp",EDGE,"E92.17"),sQuery(id+"F4.wireOp",EDGE,"E93"),sQuery(id+"F4.wireOp",EDGE,"E94")])],"isStart":false}),"instanceName":"1"})]});
            var Q34;
            Q34=makeQuery(id+"F6.boolean.opBoolean","INTERSECT",EDGE,{"derivedFrom":[makeQuery(id+"F1.opExtrude","SWEPT_FACE",FACE,{"disambiguationData":[OSD([sQuery(id+"F0.wireOp",EDGE,"E25"),sQuery(id+"F0.wireOp",EDGE,"E73")])]}),makeQuery(id+"F6.opPattern","COPY",FACE,{"derivedFrom":makeQuery(id+"F5.opExtrude","CAP_FACE",FACE,{"disambiguationData":[OSD([sQuery(id+"F4.wireOp",EDGE,"E92.0"),sQuery(id+"F4.wireOp",EDGE,"E92.1"),sQuery(id+"F4.wireOp",EDGE,"E92.2"),sQuery(id+"F4.wireOp",EDGE,"E92.3"),sQuery(id+"F4.wireOp",EDGE,"E92.4"),sQuery(id+"F4.wireOp",EDGE,"E92.5"),sQuery(id+"F4.wireOp",EDGE,"E92.6"),sQuery(id+"F4.wireOp",EDGE,"E92.7"),sQuery(id+"F4.wireOp",EDGE,"E92.8"),sQuery(id+"F4.wireOp",EDGE,"E92.9"),sQuery(id+"F4.wireOp",EDGE,"E92.10"),sQuery(id+"F4.wireOp",EDGE,"E92.11"),sQuery(id+"F4.wireOp",EDGE,"E92.12"),sQuery(id+"F4.wireOp",EDGE,"E92.13"),sQuery(id+"F4.wireOp",EDGE,"E92.14"),sQuery(id+"F4.wireOp",EDGE,"E92.15"),sQuery(id+"F4.wireOp",EDGE,"E92.16"),sQuery(id+"F4.wireOp",EDGE,"E92.17"),sQuery(id+"F4.wireOp",EDGE,"E93"),sQuery(id+"F4.wireOp",EDGE,"E94")])],"isStart":false}),"instanceName":"1"})]});
            var Q35;
            Q35=makeQuery(id+"F6.boolean.opBoolean","INTERSECT",EDGE,{"derivedFrom":[makeQuery(id+"F1.opExtrude","SWEPT_FACE",FACE,{"disambiguationData":[OSD([sQuery(id+"F0.wireOp",EDGE,"E20"),sQuery(id+"F0.wireOp",EDGE,"E81")])]}),makeQuery(id+"F6.opPattern","COPY",FACE,{"derivedFrom":makeQuery(id+"F5.opExtrude","CAP_FACE",FACE,{"disambiguationData":[OSD([sQuery(id+"F4.wireOp",EDGE,"E92.0"),sQuery(id+"F4.wireOp",EDGE,"E92.1"),sQuery(id+"F4.wireOp",EDGE,"E92.2"),sQuery(id+"F4.wireOp",EDGE,"E92.3"),sQuery(id+"F4.wireOp",EDGE,"E92.4"),sQuery(id+"F4.wireOp",EDGE,"E92.5"),sQuery(id+"F4.wireOp",EDGE,"E92.6"),sQuery(id+"F4.wireOp",EDGE,"E92.7"),sQuery(id+"F4.wireOp",EDGE,"E92.8"),sQuery(id+"F4.wireOp",EDGE,"E92.9"),sQuery(id+"F4.wireOp",EDGE,"E92.10"),sQuery(id+"F4.wireOp",EDGE,"E92.11"),sQuery(id+"F4.wireOp",EDGE,"E92.12"),sQuery(id+"F4.wireOp",EDGE,"E92.13"),sQuery(id+"F4.wireOp",EDGE,"E92.14"),sQuery(id+"F4.wireOp",EDGE,"E92.15"),sQuery(id+"F4.wireOp",EDGE,"E92.16"),sQuery(id+"F4.wireOp",EDGE,"E92.17"),sQuery(id+"F4.wireOp",EDGE,"E93"),sQuery(id+"F4.wireOp",EDGE,"E94")])],"isStart":false}),"instanceName":"1"})]});
            var Q36;
            Q36=makeQuery(id+"F6.boolean.opBoolean","INTERSECT",EDGE,{"derivedFrom":[makeQuery(id+"F1.opExtrude","SWEPT_FACE",FACE,{"disambiguationData":[OSD([sQuery(id+"F0.wireOp",EDGE,"E17"),sQuery(id+"F0.wireOp",EDGE,"E80")])]}),makeQuery(id+"F6.opPattern","COPY",FACE,{"derivedFrom":makeQuery(id+"F5.opExtrude","CAP_FACE",FACE,{"disambiguationData":[OSD([sQuery(id+"F4.wireOp",EDGE,"E92.0"),sQuery(id+"F4.wireOp",EDGE,"E92.1"),sQuery(id+"F4.wireOp",EDGE,"E92.2"),sQuery(id+"F4.wireOp",EDGE,"E92.3"),sQuery(id+"F4.wireOp",EDGE,"E92.4"),sQuery(id+"F4.wireOp",EDGE,"E92.5"),sQuery(id+"F4.wireOp",EDGE,"E92.6"),sQuery(id+"F4.wireOp",EDGE,"E92.7"),sQuery(id+"F4.wireOp",EDGE,"E92.8"),sQuery(id+"F4.wireOp",EDGE,"E92.9"),sQuery(id+"F4.wireOp",EDGE,"E92.10"),sQuery(id+"F4.wireOp",EDGE,"E92.11"),sQuery(id+"F4.wireOp",EDGE,"E92.12"),sQuery(id+"F4.wireOp",EDGE,"E92.13"),sQuery(id+"F4.wireOp",EDGE,"E92.14"),sQuery(id+"F4.wireOp",EDGE,"E92.15"),sQuery(id+"F4.wireOp",EDGE,"E92.16"),sQuery(id+"F4.wireOp",EDGE,"E92.17"),sQuery(id+"F4.wireOp",EDGE,"E93"),sQuery(id+"F4.wireOp",EDGE,"E94")])],"isStart":false}),"instanceName":"1"})]});
            var Q37;
            Q37=makeQuery(id+"F6.boolean.opBoolean","INTERSECT",EDGE,{"derivedFrom":[makeQuery(id+"F1.opExtrude","SWEPT_FACE",FACE,{"disambiguationData":[OSD([sQuery(id+"F0.wireOp",EDGE,"E13"),sQuery(id+"F0.wireOp",EDGE,"E63")])]}),makeQuery(id+"F6.opPattern","COPY",FACE,{"derivedFrom":makeQuery(id+"F5.opExtrude","CAP_FACE",FACE,{"disambiguationData":[OSD([sQuery(id+"F4.wireOp",EDGE,"E92.0"),sQuery(id+"F4.wireOp",EDGE,"E92.1"),sQuery(id+"F4.wireOp",EDGE,"E92.2"),sQuery(id+"F4.wireOp",EDGE,"E92.3"),sQuery(id+"F4.wireOp",EDGE,"E92.4"),sQuery(id+"F4.wireOp",EDGE,"E92.5"),sQuery(id+"F4.wireOp",EDGE,"E92.6"),sQuery(id+"F4.wireOp",EDGE,"E92.7"),sQuery(id+"F4.wireOp",EDGE,"E92.8"),sQuery(id+"F4.wireOp",EDGE,"E92.9"),sQuery(id+"F4.wireOp",EDGE,"E92.10"),sQuery(id+"F4.wireOp",EDGE,"E92.11"),sQuery(id+"F4.wireOp",EDGE,"E92.12"),sQuery(id+"F4.wireOp",EDGE,"E92.13"),sQuery(id+"F4.wireOp",EDGE,"E92.14"),sQuery(id+"F4.wireOp",EDGE,"E92.15"),sQuery(id+"F4.wireOp",EDGE,"E92.16"),sQuery(id+"F4.wireOp",EDGE,"E92.17"),sQuery(id+"F4.wireOp",EDGE,"E93"),sQuery(id+"F4.wireOp",EDGE,"E94")])],"isStart":false}),"instanceName":"1"})]});
            var Q38;
            Q38=makeQuery(id+"F6.boolean.opBoolean","INTERSECT",EDGE,{"derivedFrom":[makeQuery(id+"F1.opExtrude","SWEPT_FACE",FACE,{"disambiguationData":[OSD([sQuery(id+"F0.wireOp",EDGE,"E9"),sQuery(id+"F0.wireOp",EDGE,"E60")])]}),makeQuery(id+"F6.opPattern","COPY",FACE,{"derivedFrom":makeQuery(id+"F5.opExtrude","CAP_FACE",FACE,{"disambiguationData":[OSD([sQuery(id+"F4.wireOp",EDGE,"E92.0"),sQuery(id+"F4.wireOp",EDGE,"E92.1"),sQuery(id+"F4.wireOp",EDGE,"E92.2"),sQuery(id+"F4.wireOp",EDGE,"E92.3"),sQuery(id+"F4.wireOp",EDGE,"E92.4"),sQuery(id+"F4.wireOp",EDGE,"E92.5"),sQuery(id+"F4.wireOp",EDGE,"E92.6"),sQuery(id+"F4.wireOp",EDGE,"E92.7"),sQuery(id+"F4.wireOp",EDGE,"E92.8"),sQuery(id+"F4.wireOp",EDGE,"E92.9"),sQuery(id+"F4.wireOp",EDGE,"E92.10"),sQuery(id+"F4.wireOp",EDGE,"E92.11"),sQuery(id+"F4.wireOp",EDGE,"E92.12"),sQuery(id+"F4.wireOp",EDGE,"E92.13"),sQuery(id+"F4.wireOp",EDGE,"E92.14"),sQuery(id+"F4.wireOp",EDGE,"E92.15"),sQuery(id+"F4.wireOp",EDGE,"E92.16"),sQuery(id+"F4.wireOp",EDGE,"E92.17"),sQuery(id+"F4.wireOp",EDGE,"E93"),sQuery(id+"F4.wireOp",EDGE,"E94")])],"isStart":false}),"instanceName":"1"})]});
            fillet(context, id + "F12", {"entities" : qUnion([Q0, Q1, Q2, Q3, Q4, Q5, Q6, Q7, Q8, Q9, Q10, Q11, Q12, Q13, Q14, Q15, Q16, Q17, Q18, Q19, Q20, Q21, Q22, Q23, Q24, Q25, Q26, Q27, Q28, Q29, Q30, Q31, Q32, Q33, Q34, Q35, Q36, Q37, Q38]), "radius" : 12.7 * mm, "tangentPropagation" : true, "allowEdgeOverflow" : false});
        }
        {
            var Q0;
            Q0=makeQuery(id+"F6.boolean.opBoolean","INTERSECT",EDGE,{"derivedFrom":[makeQuery(id+"F1.opExtrude","SWEPT_FACE",FACE,{"disambiguationData":[OSD([sQuery(id+"F0.wireOp",EDGE,"E61")])]}),makeQuery(id+"F6.opPattern","COPY",FACE,{"derivedFrom":makeQuery(id+"F5.opExtrude","CAP_FACE",FACE,{"disambiguationData":[OSD([sQuery(id+"F4.wireOp",EDGE,"E92.0"),sQuery(id+"F4.wireOp",EDGE,"E92.1"),sQuery(id+"F4.wireOp",EDGE,"E92.2"),sQuery(id+"F4.wireOp",EDGE,"E92.3"),sQuery(id+"F4.wireOp",EDGE,"E92.4"),sQuery(id+"F4.wireOp",EDGE,"E92.5"),sQuery(id+"F4.wireOp",EDGE,"E92.6"),sQuery(id+"F4.wireOp",EDGE,"E92.7"),sQuery(id+"F4.wireOp",EDGE,"E92.8"),sQuery(id+"F4.wireOp",EDGE,"E92.9"),sQuery(id+"F4.wireOp",EDGE,"E92.10"),sQuery(id+"F4.wireOp",EDGE,"E92.11"),sQuery(id+"F4.wireOp",EDGE,"E92.12"),sQuery(id+"F4.wireOp",EDGE,"E92.13"),sQuery(id+"F4.wireOp",EDGE,"E92.14"),sQuery(id+"F4.wireOp",EDGE,"E92.15"),sQuery(id+"F4.wireOp",EDGE,"E92.16"),sQuery(id+"F4.wireOp",EDGE,"E92.17"),sQuery(id+"F4.wireOp",EDGE,"E93"),sQuery(id+"F4.wireOp",EDGE,"E94")])],"isStart":false}),"instanceName":"1"})]});
            var Q1;
            Q1=makeQuery(id+"F6.boolean.opBoolean","INTERSECT",EDGE,{"derivedFrom":[makeQuery(id+"F1.opExtrude","SWEPT_FACE",FACE,{"disambiguationData":[OSD([sQuery(id+"F0.wireOp",EDGE,"E64")])]}),makeQuery(id+"F6.opPattern","COPY",FACE,{"derivedFrom":makeQuery(id+"F5.opExtrude","CAP_FACE",FACE,{"disambiguationData":[OSD([sQuery(id+"F4.wireOp",EDGE,"E92.0"),sQuery(id+"F4.wireOp",EDGE,"E92.1"),sQuery(id+"F4.wireOp",EDGE,"E92.2"),sQuery(id+"F4.wireOp",EDGE,"E92.3"),sQuery(id+"F4.wireOp",EDGE,"E92.4"),sQuery(id+"F4.wireOp",EDGE,"E92.5"),sQuery(id+"F4.wireOp",EDGE,"E92.6"),sQuery(id+"F4.wireOp",EDGE,"E92.7"),sQuery(id+"F4.wireOp",EDGE,"E92.8"),sQuery(id+"F4.wireOp",EDGE,"E92.9"),sQuery(id+"F4.wireOp",EDGE,"E92.10"),sQuery(id+"F4.wireOp",EDGE,"E92.11"),sQuery(id+"F4.wireOp",EDGE,"E92.12"),sQuery(id+"F4.wireOp",EDGE,"E92.13"),sQuery(id+"F4.wireOp",EDGE,"E92.14"),sQuery(id+"F4.wireOp",EDGE,"E92.15"),sQuery(id+"F4.wireOp",EDGE,"E92.16"),sQuery(id+"F4.wireOp",EDGE,"E92.17"),sQuery(id+"F4.wireOp",EDGE,"E93"),sQuery(id+"F4.wireOp",EDGE,"E94")])],"isStart":false}),"instanceName":"1"})]});
            var Q2;
            Q2=makeQuery(id+"F6.boolean.opBoolean","INTERSECT",EDGE,{"derivedFrom":[makeQuery(id+"F1.opExtrude","SWEPT_FACE",FACE,{"disambiguationData":[OSD([sQuery(id+"F0.wireOp",EDGE,"E79")])]}),makeQuery(id+"F6.opPattern","COPY",FACE,{"derivedFrom":makeQuery(id+"F5.opExtrude","CAP_FACE",FACE,{"disambiguationData":[OSD([sQuery(id+"F4.wireOp",EDGE,"E92.0"),sQuery(id+"F4.wireOp",EDGE,"E92.1"),sQuery(id+"F4.wireOp",EDGE,"E92.2"),sQuery(id+"F4.wireOp",EDGE,"E92.3"),sQuery(id+"F4.wireOp",EDGE,"E92.4"),sQuery(id+"F4.wireOp",EDGE,"E92.5"),sQuery(id+"F4.wireOp",EDGE,"E92.6"),sQuery(id+"F4.wireOp",EDGE,"E92.7"),sQuery(id+"F4.wireOp",EDGE,"E92.8"),sQuery(id+"F4.wireOp",EDGE,"E92.9"),sQuery(id+"F4.wireOp",EDGE,"E92.10"),sQuery(id+"F4.wireOp",EDGE,"E92.11"),sQuery(id+"F4.wireOp",EDGE,"E92.12"),sQuery(id+"F4.wireOp",EDGE,"E92.13"),sQuery(id+"F4.wireOp",EDGE,"E92.14"),sQuery(id+"F4.wireOp",EDGE,"E92.15"),sQuery(id+"F4.wireOp",EDGE,"E92.16"),sQuery(id+"F4.wireOp",EDGE,"E92.17"),sQuery(id+"F4.wireOp",EDGE,"E93"),sQuery(id+"F4.wireOp",EDGE,"E94")])],"isStart":false}),"instanceName":"1"})]});
            var Q3;
            Q3=makeQuery(id+"F6.boolean.opBoolean","INTERSECT",EDGE,{"derivedFrom":[makeQuery(id+"F1.opExtrude","SWEPT_FACE",FACE,{"disambiguationData":[OSD([sQuery(id+"F0.wireOp",EDGE,"E66")])]}),makeQuery(id+"F6.opPattern","COPY",FACE,{"derivedFrom":makeQuery(id+"F5.opExtrude","CAP_FACE",FACE,{"disambiguationData":[OSD([sQuery(id+"F4.wireOp",EDGE,"E92.0"),sQuery(id+"F4.wireOp",EDGE,"E92.1"),sQuery(id+"F4.wireOp",EDGE,"E92.2"),sQuery(id+"F4.wireOp",EDGE,"E92.3"),sQuery(id+"F4.wireOp",EDGE,"E92.4"),sQuery(id+"F4.wireOp",EDGE,"E92.5"),sQuery(id+"F4.wireOp",EDGE,"E92.6"),sQuery(id+"F4.wireOp",EDGE,"E92.7"),sQuery(id+"F4.wireOp",EDGE,"E92.8"),sQuery(id+"F4.wireOp",EDGE,"E92.9"),sQuery(id+"F4.wireOp",EDGE,"E92.10"),sQuery(id+"F4.wireOp",EDGE,"E92.11"),sQuery(id+"F4.wireOp",EDGE,"E92.12"),sQuery(id+"F4.wireOp",EDGE,"E92.13"),sQuery(id+"F4.wireOp",EDGE,"E92.14"),sQuery(id+"F4.wireOp",EDGE,"E92.15"),sQuery(id+"F4.wireOp",EDGE,"E92.16"),sQuery(id+"F4.wireOp",EDGE,"E92.17"),sQuery(id+"F4.wireOp",EDGE,"E93"),sQuery(id+"F4.wireOp",EDGE,"E94")])],"isStart":false}),"instanceName":"1"})]});
            var Q4;
            Q4=makeQuery(id+"F6.boolean.opBoolean","INTERSECT",EDGE,{"derivedFrom":[makeQuery(id+"F1.opExtrude","SWEPT_FACE",FACE,{"disambiguationData":[OSD([sQuery(id+"F0.wireOp",EDGE,"E84")])]}),makeQuery(id+"F6.opPattern","COPY",FACE,{"derivedFrom":makeQuery(id+"F5.opExtrude","CAP_FACE",FACE,{"disambiguationData":[OSD([sQuery(id+"F4.wireOp",EDGE,"E92.0"),sQuery(id+"F4.wireOp",EDGE,"E92.1"),sQuery(id+"F4.wireOp",EDGE,"E92.2"),sQuery(id+"F4.wireOp",EDGE,"E92.3"),sQuery(id+"F4.wireOp",EDGE,"E92.4"),sQuery(id+"F4.wireOp",EDGE,"E92.5"),sQuery(id+"F4.wireOp",EDGE,"E92.6"),sQuery(id+"F4.wireOp",EDGE,"E92.7"),sQuery(id+"F4.wireOp",EDGE,"E92.8"),sQuery(id+"F4.wireOp",EDGE,"E92.9"),sQuery(id+"F4.wireOp",EDGE,"E92.10"),sQuery(id+"F4.wireOp",EDGE,"E92.11"),sQuery(id+"F4.wireOp",EDGE,"E92.12"),sQuery(id+"F4.wireOp",EDGE,"E92.13"),sQuery(id+"F4.wireOp",EDGE,"E92.14"),sQuery(id+"F4.wireOp",EDGE,"E92.15"),sQuery(id+"F4.wireOp",EDGE,"E92.16"),sQuery(id+"F4.wireOp",EDGE,"E92.17"),sQuery(id+"F4.wireOp",EDGE,"E93"),sQuery(id+"F4.wireOp",EDGE,"E94")])],"isStart":false}),"instanceName":"1"})]});
            var Q5;
            Q5=makeQuery(id+"F6.boolean.opBoolean","INTERSECT",EDGE,{"derivedFrom":[makeQuery(id+"F1.opExtrude","SWEPT_FACE",FACE,{"disambiguationData":[OSD([sQuery(id+"F0.wireOp",EDGE,"E86")])]}),makeQuery(id+"F6.opPattern","COPY",FACE,{"derivedFrom":makeQuery(id+"F5.opExtrude","CAP_FACE",FACE,{"disambiguationData":[OSD([sQuery(id+"F4.wireOp",EDGE,"E92.0"),sQuery(id+"F4.wireOp",EDGE,"E92.1"),sQuery(id+"F4.wireOp",EDGE,"E92.2"),sQuery(id+"F4.wireOp",EDGE,"E92.3"),sQuery(id+"F4.wireOp",EDGE,"E92.4"),sQuery(id+"F4.wireOp",EDGE,"E92.5"),sQuery(id+"F4.wireOp",EDGE,"E92.6"),sQuery(id+"F4.wireOp",EDGE,"E92.7"),sQuery(id+"F4.wireOp",EDGE,"E92.8"),sQuery(id+"F4.wireOp",EDGE,"E92.9"),sQuery(id+"F4.wireOp",EDGE,"E92.10"),sQuery(id+"F4.wireOp",EDGE,"E92.11"),sQuery(id+"F4.wireOp",EDGE,"E92.12"),sQuery(id+"F4.wireOp",EDGE,"E92.13"),sQuery(id+"F4.wireOp",EDGE,"E92.14"),sQuery(id+"F4.wireOp",EDGE,"E92.15"),sQuery(id+"F4.wireOp",EDGE,"E92.16"),sQuery(id+"F4.wireOp",EDGE,"E92.17"),sQuery(id+"F4.wireOp",EDGE,"E93"),sQuery(id+"F4.wireOp",EDGE,"E94")])],"isStart":false}),"instanceName":"1"})]});
            var Q6;
            Q6=makeQuery(id+"F6.boolean.opBoolean","INTERSECT",EDGE,{"derivedFrom":[makeQuery(id+"F1.opExtrude","SWEPT_FACE",FACE,{"disambiguationData":[OSD([sQuery(id+"F0.wireOp",EDGE,"E88")])]}),makeQuery(id+"F6.opPattern","COPY",FACE,{"derivedFrom":makeQuery(id+"F5.opExtrude","CAP_FACE",FACE,{"disambiguationData":[OSD([sQuery(id+"F4.wireOp",EDGE,"E92.0"),sQuery(id+"F4.wireOp",EDGE,"E92.1"),sQuery(id+"F4.wireOp",EDGE,"E92.2"),sQuery(id+"F4.wireOp",EDGE,"E92.3"),sQuery(id+"F4.wireOp",EDGE,"E92.4"),sQuery(id+"F4.wireOp",EDGE,"E92.5"),sQuery(id+"F4.wireOp",EDGE,"E92.6"),sQuery(id+"F4.wireOp",EDGE,"E92.7"),sQuery(id+"F4.wireOp",EDGE,"E92.8"),sQuery(id+"F4.wireOp",EDGE,"E92.9"),sQuery(id+"F4.wireOp",EDGE,"E92.10"),sQuery(id+"F4.wireOp",EDGE,"E92.11"),sQuery(id+"F4.wireOp",EDGE,"E92.12"),sQuery(id+"F4.wireOp",EDGE,"E92.13"),sQuery(id+"F4.wireOp",EDGE,"E92.14"),sQuery(id+"F4.wireOp",EDGE,"E92.15"),sQuery(id+"F4.wireOp",EDGE,"E92.16"),sQuery(id+"F4.wireOp",EDGE,"E92.17"),sQuery(id+"F4.wireOp",EDGE,"E93"),sQuery(id+"F4.wireOp",EDGE,"E94")])],"isStart":false}),"instanceName":"1"})]});
            var Q7;
            Q7=makeQuery(id+"F6.boolean.opBoolean","INTERSECT",EDGE,{"derivedFrom":[makeQuery(id+"F1.opExtrude","SWEPT_FACE",FACE,{"disambiguationData":[OSD([sQuery(id+"F0.wireOp",EDGE,"E68")])]}),makeQuery(id+"F6.opPattern","COPY",FACE,{"derivedFrom":makeQuery(id+"F5.opExtrude","CAP_FACE",FACE,{"disambiguationData":[OSD([sQuery(id+"F4.wireOp",EDGE,"E92.0"),sQuery(id+"F4.wireOp",EDGE,"E92.1"),sQuery(id+"F4.wireOp",EDGE,"E92.2"),sQuery(id+"F4.wireOp",EDGE,"E92.3"),sQuery(id+"F4.wireOp",EDGE,"E92.4"),sQuery(id+"F4.wireOp",EDGE,"E92.5"),sQuery(id+"F4.wireOp",EDGE,"E92.6"),sQuery(id+"F4.wireOp",EDGE,"E92.7"),sQuery(id+"F4.wireOp",EDGE,"E92.8"),sQuery(id+"F4.wireOp",EDGE,"E92.9"),sQuery(id+"F4.wireOp",EDGE,"E92.10"),sQuery(id+"F4.wireOp",EDGE,"E92.11"),sQuery(id+"F4.wireOp",EDGE,"E92.12"),sQuery(id+"F4.wireOp",EDGE,"E92.13"),sQuery(id+"F4.wireOp",EDGE,"E92.14"),sQuery(id+"F4.wireOp",EDGE,"E92.15"),sQuery(id+"F4.wireOp",EDGE,"E92.16"),sQuery(id+"F4.wireOp",EDGE,"E92.17"),sQuery(id+"F4.wireOp",EDGE,"E93"),sQuery(id+"F4.wireOp",EDGE,"E94")])],"isStart":false}),"instanceName":"1"})]});
            var Q8;
            Q8=makeQuery(id+"F6.boolean.opBoolean","INTERSECT",EDGE,{"derivedFrom":[makeQuery(id+"F1.opExtrude","SWEPT_FACE",FACE,{"disambiguationData":[OSD([sQuery(id+"F0.wireOp",EDGE,"E91")])]}),makeQuery(id+"F6.opPattern","COPY",FACE,{"derivedFrom":makeQuery(id+"F5.opExtrude","CAP_FACE",FACE,{"disambiguationData":[OSD([sQuery(id+"F4.wireOp",EDGE,"E92.0"),sQuery(id+"F4.wireOp",EDGE,"E92.1"),sQuery(id+"F4.wireOp",EDGE,"E92.2"),sQuery(id+"F4.wireOp",EDGE,"E92.3"),sQuery(id+"F4.wireOp",EDGE,"E92.4"),sQuery(id+"F4.wireOp",EDGE,"E92.5"),sQuery(id+"F4.wireOp",EDGE,"E92.6"),sQuery(id+"F4.wireOp",EDGE,"E92.7"),sQuery(id+"F4.wireOp",EDGE,"E92.8"),sQuery(id+"F4.wireOp",EDGE,"E92.9"),sQuery(id+"F4.wireOp",EDGE,"E92.10"),sQuery(id+"F4.wireOp",EDGE,"E92.11"),sQuery(id+"F4.wireOp",EDGE,"E92.12"),sQuery(id+"F4.wireOp",EDGE,"E92.13"),sQuery(id+"F4.wireOp",EDGE,"E92.14"),sQuery(id+"F4.wireOp",EDGE,"E92.15"),sQuery(id+"F4.wireOp",EDGE,"E92.16"),sQuery(id+"F4.wireOp",EDGE,"E92.17"),sQuery(id+"F4.wireOp",EDGE,"E93"),sQuery(id+"F4.wireOp",EDGE,"E94")])],"isStart":false}),"instanceName":"1"})]});
            var Q9;
            Q9=makeQuery(id+"F6.boolean.opBoolean","INTERSECT",EDGE,{"derivedFrom":[makeQuery(id+"F1.opExtrude","SWEPT_FACE",FACE,{"disambiguationData":[OSD([sQuery(id+"F0.wireOp",EDGE,"E71")])]}),makeQuery(id+"F6.opPattern","COPY",FACE,{"derivedFrom":makeQuery(id+"F5.opExtrude","CAP_FACE",FACE,{"disambiguationData":[OSD([sQuery(id+"F4.wireOp",EDGE,"E92.0"),sQuery(id+"F4.wireOp",EDGE,"E92.1"),sQuery(id+"F4.wireOp",EDGE,"E92.2"),sQuery(id+"F4.wireOp",EDGE,"E92.3"),sQuery(id+"F4.wireOp",EDGE,"E92.4"),sQuery(id+"F4.wireOp",EDGE,"E92.5"),sQuery(id+"F4.wireOp",EDGE,"E92.6"),sQuery(id+"F4.wireOp",EDGE,"E92.7"),sQuery(id+"F4.wireOp",EDGE,"E92.8"),sQuery(id+"F4.wireOp",EDGE,"E92.9"),sQuery(id+"F4.wireOp",EDGE,"E92.10"),sQuery(id+"F4.wireOp",EDGE,"E92.11"),sQuery(id+"F4.wireOp",EDGE,"E92.12"),sQuery(id+"F4.wireOp",EDGE,"E92.13"),sQuery(id+"F4.wireOp",EDGE,"E92.14"),sQuery(id+"F4.wireOp",EDGE,"E92.15"),sQuery(id+"F4.wireOp",EDGE,"E92.16"),sQuery(id+"F4.wireOp",EDGE,"E92.17"),sQuery(id+"F4.wireOp",EDGE,"E93"),sQuery(id+"F4.wireOp",EDGE,"E94")])],"isStart":false}),"instanceName":"1"})]});
            var Q10;
            Q10=makeQuery(id+"F6.boolean.opBoolean","INTERSECT",EDGE,{"derivedFrom":[makeQuery(id+"F1.opExtrude","SWEPT_FACE",FACE,{"disambiguationData":[OSD([sQuery(id+"F0.wireOp",EDGE,"E71")])]}),makeQuery(id+"F5.opExtrude","CAP_FACE",FACE,{"disambiguationData":[OSD([sQuery(id+"F4.wireOp",EDGE,"E92.0"),sQuery(id+"F4.wireOp",EDGE,"E92.1"),sQuery(id+"F4.wireOp",EDGE,"E92.2"),sQuery(id+"F4.wireOp",EDGE,"E92.3"),sQuery(id+"F4.wireOp",EDGE,"E92.4"),sQuery(id+"F4.wireOp",EDGE,"E92.5"),sQuery(id+"F4.wireOp",EDGE,"E92.6"),sQuery(id+"F4.wireOp",EDGE,"E92.7"),sQuery(id+"F4.wireOp",EDGE,"E92.8"),sQuery(id+"F4.wireOp",EDGE,"E92.9"),sQuery(id+"F4.wireOp",EDGE,"E92.10"),sQuery(id+"F4.wireOp",EDGE,"E92.11"),sQuery(id+"F4.wireOp",EDGE,"E92.12"),sQuery(id+"F4.wireOp",EDGE,"E92.13"),sQuery(id+"F4.wireOp",EDGE,"E92.14"),sQuery(id+"F4.wireOp",EDGE,"E92.15"),sQuery(id+"F4.wireOp",EDGE,"E92.16"),sQuery(id+"F4.wireOp",EDGE,"E92.17"),sQuery(id+"F4.wireOp",EDGE,"E93"),sQuery(id+"F4.wireOp",EDGE,"E94")])],"isStart":false})]});
            var Q11;
            Q11=makeQuery(id+"F6.boolean.opBoolean","INTERSECT",EDGE,{"derivedFrom":[makeQuery(id+"F1.opExtrude","SWEPT_FACE",FACE,{"disambiguationData":[OSD([sQuery(id+"F0.wireOp",EDGE,"E91")])]}),makeQuery(id+"F5.opExtrude","CAP_FACE",FACE,{"disambiguationData":[OSD([sQuery(id+"F4.wireOp",EDGE,"E92.0"),sQuery(id+"F4.wireOp",EDGE,"E92.1"),sQuery(id+"F4.wireOp",EDGE,"E92.2"),sQuery(id+"F4.wireOp",EDGE,"E92.3"),sQuery(id+"F4.wireOp",EDGE,"E92.4"),sQuery(id+"F4.wireOp",EDGE,"E92.5"),sQuery(id+"F4.wireOp",EDGE,"E92.6"),sQuery(id+"F4.wireOp",EDGE,"E92.7"),sQuery(id+"F4.wireOp",EDGE,"E92.8"),sQuery(id+"F4.wireOp",EDGE,"E92.9"),sQuery(id+"F4.wireOp",EDGE,"E92.10"),sQuery(id+"F4.wireOp",EDGE,"E92.11"),sQuery(id+"F4.wireOp",EDGE,"E92.12"),sQuery(id+"F4.wireOp",EDGE,"E92.13"),sQuery(id+"F4.wireOp",EDGE,"E92.14"),sQuery(id+"F4.wireOp",EDGE,"E92.15"),sQuery(id+"F4.wireOp",EDGE,"E92.16"),sQuery(id+"F4.wireOp",EDGE,"E92.17"),sQuery(id+"F4.wireOp",EDGE,"E93"),sQuery(id+"F4.wireOp",EDGE,"E94")])],"isStart":false})]});
            var Q12;
            Q12=makeQuery(id+"F6.boolean.opBoolean","INTERSECT",EDGE,{"derivedFrom":[makeQuery(id+"F1.opExtrude","SWEPT_FACE",FACE,{"disambiguationData":[OSD([sQuery(id+"F0.wireOp",EDGE,"E68")])]}),makeQuery(id+"F5.opExtrude","CAP_FACE",FACE,{"disambiguationData":[OSD([sQuery(id+"F4.wireOp",EDGE,"E92.0"),sQuery(id+"F4.wireOp",EDGE,"E92.1"),sQuery(id+"F4.wireOp",EDGE,"E92.2"),sQuery(id+"F4.wireOp",EDGE,"E92.3"),sQuery(id+"F4.wireOp",EDGE,"E92.4"),sQuery(id+"F4.wireOp",EDGE,"E92.5"),sQuery(id+"F4.wireOp",EDGE,"E92.6"),sQuery(id+"F4.wireOp",EDGE,"E92.7"),sQuery(id+"F4.wireOp",EDGE,"E92.8"),sQuery(id+"F4.wireOp",EDGE,"E92.9"),sQuery(id+"F4.wireOp",EDGE,"E92.10"),sQuery(id+"F4.wireOp",EDGE,"E92.11"),sQuery(id+"F4.wireOp",EDGE,"E92.12"),sQuery(id+"F4.wireOp",EDGE,"E92.13"),sQuery(id+"F4.wireOp",EDGE,"E92.14"),sQuery(id+"F4.wireOp",EDGE,"E92.15"),sQuery(id+"F4.wireOp",EDGE,"E92.16"),sQuery(id+"F4.wireOp",EDGE,"E92.17"),sQuery(id+"F4.wireOp",EDGE,"E93"),sQuery(id+"F4.wireOp",EDGE,"E94")])],"isStart":false})]});
            var Q13;
            Q13=makeQuery(id+"F6.boolean.opBoolean","INTERSECT",EDGE,{"derivedFrom":[makeQuery(id+"F1.opExtrude","SWEPT_FACE",FACE,{"disambiguationData":[OSD([sQuery(id+"F0.wireOp",EDGE,"E88")])]}),makeQuery(id+"F5.opExtrude","CAP_FACE",FACE,{"disambiguationData":[OSD([sQuery(id+"F4.wireOp",EDGE,"E92.0"),sQuery(id+"F4.wireOp",EDGE,"E92.1"),sQuery(id+"F4.wireOp",EDGE,"E92.2"),sQuery(id+"F4.wireOp",EDGE,"E92.3"),sQuery(id+"F4.wireOp",EDGE,"E92.4"),sQuery(id+"F4.wireOp",EDGE,"E92.5"),sQuery(id+"F4.wireOp",EDGE,"E92.6"),sQuery(id+"F4.wireOp",EDGE,"E92.7"),sQuery(id+"F4.wireOp",EDGE,"E92.8"),sQuery(id+"F4.wireOp",EDGE,"E92.9"),sQuery(id+"F4.wireOp",EDGE,"E92.10"),sQuery(id+"F4.wireOp",EDGE,"E92.11"),sQuery(id+"F4.wireOp",EDGE,"E92.12"),sQuery(id+"F4.wireOp",EDGE,"E92.13"),sQuery(id+"F4.wireOp",EDGE,"E92.14"),sQuery(id+"F4.wireOp",EDGE,"E92.15"),sQuery(id+"F4.wireOp",EDGE,"E92.16"),sQuery(id+"F4.wireOp",EDGE,"E92.17"),sQuery(id+"F4.wireOp",EDGE,"E93"),sQuery(id+"F4.wireOp",EDGE,"E94")])],"isStart":false})]});
            var Q14;
            Q14=makeQuery(id+"F6.boolean.opBoolean","INTERSECT",EDGE,{"derivedFrom":[makeQuery(id+"F1.opExtrude","SWEPT_FACE",FACE,{"disambiguationData":[OSD([sQuery(id+"F0.wireOp",EDGE,"E86")])]}),makeQuery(id+"F5.opExtrude","CAP_FACE",FACE,{"disambiguationData":[OSD([sQuery(id+"F4.wireOp",EDGE,"E92.0"),sQuery(id+"F4.wireOp",EDGE,"E92.1"),sQuery(id+"F4.wireOp",EDGE,"E92.2"),sQuery(id+"F4.wireOp",EDGE,"E92.3"),sQuery(id+"F4.wireOp",EDGE,"E92.4"),sQuery(id+"F4.wireOp",EDGE,"E92.5"),sQuery(id+"F4.wireOp",EDGE,"E92.6"),sQuery(id+"F4.wireOp",EDGE,"E92.7"),sQuery(id+"F4.wireOp",EDGE,"E92.8"),sQuery(id+"F4.wireOp",EDGE,"E92.9"),sQuery(id+"F4.wireOp",EDGE,"E92.10"),sQuery(id+"F4.wireOp",EDGE,"E92.11"),sQuery(id+"F4.wireOp",EDGE,"E92.12"),sQuery(id+"F4.wireOp",EDGE,"E92.13"),sQuery(id+"F4.wireOp",EDGE,"E92.14"),sQuery(id+"F4.wireOp",EDGE,"E92.15"),sQuery(id+"F4.wireOp",EDGE,"E92.16"),sQuery(id+"F4.wireOp",EDGE,"E92.17"),sQuery(id+"F4.wireOp",EDGE,"E93"),sQuery(id+"F4.wireOp",EDGE,"E94")])],"isStart":false})]});
            var Q15;
            Q15=makeQuery(id+"F6.boolean.opBoolean","INTERSECT",EDGE,{"derivedFrom":[makeQuery(id+"F1.opExtrude","SWEPT_FACE",FACE,{"disambiguationData":[OSD([sQuery(id+"F0.wireOp",EDGE,"E84")])]}),makeQuery(id+"F5.opExtrude","CAP_FACE",FACE,{"disambiguationData":[OSD([sQuery(id+"F4.wireOp",EDGE,"E92.0"),sQuery(id+"F4.wireOp",EDGE,"E92.1"),sQuery(id+"F4.wireOp",EDGE,"E92.2"),sQuery(id+"F4.wireOp",EDGE,"E92.3"),sQuery(id+"F4.wireOp",EDGE,"E92.4"),sQuery(id+"F4.wireOp",EDGE,"E92.5"),sQuery(id+"F4.wireOp",EDGE,"E92.6"),sQuery(id+"F4.wireOp",EDGE,"E92.7"),sQuery(id+"F4.wireOp",EDGE,"E92.8"),sQuery(id+"F4.wireOp",EDGE,"E92.9"),sQuery(id+"F4.wireOp",EDGE,"E92.10"),sQuery(id+"F4.wireOp",EDGE,"E92.11"),sQuery(id+"F4.wireOp",EDGE,"E92.12"),sQuery(id+"F4.wireOp",EDGE,"E92.13"),sQuery(id+"F4.wireOp",EDGE,"E92.14"),sQuery(id+"F4.wireOp",EDGE,"E92.15"),sQuery(id+"F4.wireOp",EDGE,"E92.16"),sQuery(id+"F4.wireOp",EDGE,"E92.17"),sQuery(id+"F4.wireOp",EDGE,"E93"),sQuery(id+"F4.wireOp",EDGE,"E94")])],"isStart":false})]});
            var Q16;
            Q16=makeQuery(id+"F6.boolean.opBoolean","INTERSECT",EDGE,{"derivedFrom":[makeQuery(id+"F1.opExtrude","SWEPT_FACE",FACE,{"disambiguationData":[OSD([sQuery(id+"F0.wireOp",EDGE,"E66")])]}),makeQuery(id+"F5.opExtrude","CAP_FACE",FACE,{"disambiguationData":[OSD([sQuery(id+"F4.wireOp",EDGE,"E92.0"),sQuery(id+"F4.wireOp",EDGE,"E92.1"),sQuery(id+"F4.wireOp",EDGE,"E92.2"),sQuery(id+"F4.wireOp",EDGE,"E92.3"),sQuery(id+"F4.wireOp",EDGE,"E92.4"),sQuery(id+"F4.wireOp",EDGE,"E92.5"),sQuery(id+"F4.wireOp",EDGE,"E92.6"),sQuery(id+"F4.wireOp",EDGE,"E92.7"),sQuery(id+"F4.wireOp",EDGE,"E92.8"),sQuery(id+"F4.wireOp",EDGE,"E92.9"),sQuery(id+"F4.wireOp",EDGE,"E92.10"),sQuery(id+"F4.wireOp",EDGE,"E92.11"),sQuery(id+"F4.wireOp",EDGE,"E92.12"),sQuery(id+"F4.wireOp",EDGE,"E92.13"),sQuery(id+"F4.wireOp",EDGE,"E92.14"),sQuery(id+"F4.wireOp",EDGE,"E92.15"),sQuery(id+"F4.wireOp",EDGE,"E92.16"),sQuery(id+"F4.wireOp",EDGE,"E92.17"),sQuery(id+"F4.wireOp",EDGE,"E93"),sQuery(id+"F4.wireOp",EDGE,"E94")])],"isStart":false})]});
            var Q17;
            Q17=makeQuery(id+"F6.boolean.opBoolean","INTERSECT",EDGE,{"derivedFrom":[makeQuery(id+"F1.opExtrude","SWEPT_FACE",FACE,{"disambiguationData":[OSD([sQuery(id+"F0.wireOp",EDGE,"E79")])]}),makeQuery(id+"F5.opExtrude","CAP_FACE",FACE,{"disambiguationData":[OSD([sQuery(id+"F4.wireOp",EDGE,"E92.0"),sQuery(id+"F4.wireOp",EDGE,"E92.1"),sQuery(id+"F4.wireOp",EDGE,"E92.2"),sQuery(id+"F4.wireOp",EDGE,"E92.3"),sQuery(id+"F4.wireOp",EDGE,"E92.4"),sQuery(id+"F4.wireOp",EDGE,"E92.5"),sQuery(id+"F4.wireOp",EDGE,"E92.6"),sQuery(id+"F4.wireOp",EDGE,"E92.7"),sQuery(id+"F4.wireOp",EDGE,"E92.8"),sQuery(id+"F4.wireOp",EDGE,"E92.9"),sQuery(id+"F4.wireOp",EDGE,"E92.10"),sQuery(id+"F4.wireOp",EDGE,"E92.11"),sQuery(id+"F4.wireOp",EDGE,"E92.12"),sQuery(id+"F4.wireOp",EDGE,"E92.13"),sQuery(id+"F4.wireOp",EDGE,"E92.14"),sQuery(id+"F4.wireOp",EDGE,"E92.15"),sQuery(id+"F4.wireOp",EDGE,"E92.16"),sQuery(id+"F4.wireOp",EDGE,"E92.17"),sQuery(id+"F4.wireOp",EDGE,"E93"),sQuery(id+"F4.wireOp",EDGE,"E94")])],"isStart":false})]});
            var Q18;
            Q18=makeQuery(id+"F6.boolean.opBoolean","INTERSECT",EDGE,{"derivedFrom":[makeQuery(id+"F1.opExtrude","SWEPT_FACE",FACE,{"disambiguationData":[OSD([sQuery(id+"F0.wireOp",EDGE,"E64")])]}),makeQuery(id+"F5.opExtrude","CAP_FACE",FACE,{"disambiguationData":[OSD([sQuery(id+"F4.wireOp",EDGE,"E92.0"),sQuery(id+"F4.wireOp",EDGE,"E92.1"),sQuery(id+"F4.wireOp",EDGE,"E92.2"),sQuery(id+"F4.wireOp",EDGE,"E92.3"),sQuery(id+"F4.wireOp",EDGE,"E92.4"),sQuery(id+"F4.wireOp",EDGE,"E92.5"),sQuery(id+"F4.wireOp",EDGE,"E92.6"),sQuery(id+"F4.wireOp",EDGE,"E92.7"),sQuery(id+"F4.wireOp",EDGE,"E92.8"),sQuery(id+"F4.wireOp",EDGE,"E92.9"),sQuery(id+"F4.wireOp",EDGE,"E92.10"),sQuery(id+"F4.wireOp",EDGE,"E92.11"),sQuery(id+"F4.wireOp",EDGE,"E92.12"),sQuery(id+"F4.wireOp",EDGE,"E92.13"),sQuery(id+"F4.wireOp",EDGE,"E92.14"),sQuery(id+"F4.wireOp",EDGE,"E92.15"),sQuery(id+"F4.wireOp",EDGE,"E92.16"),sQuery(id+"F4.wireOp",EDGE,"E92.17"),sQuery(id+"F4.wireOp",EDGE,"E93"),sQuery(id+"F4.wireOp",EDGE,"E94")])],"isStart":false})]});
            var Q19;
            Q19=makeQuery(id+"F6.boolean.opBoolean","INTERSECT",EDGE,{"derivedFrom":[makeQuery(id+"F1.opExtrude","SWEPT_FACE",FACE,{"disambiguationData":[OSD([sQuery(id+"F0.wireOp",EDGE,"E61")])]}),makeQuery(id+"F5.opExtrude","CAP_FACE",FACE,{"disambiguationData":[OSD([sQuery(id+"F4.wireOp",EDGE,"E92.0"),sQuery(id+"F4.wireOp",EDGE,"E92.1"),sQuery(id+"F4.wireOp",EDGE,"E92.2"),sQuery(id+"F4.wireOp",EDGE,"E92.3"),sQuery(id+"F4.wireOp",EDGE,"E92.4"),sQuery(id+"F4.wireOp",EDGE,"E92.5"),sQuery(id+"F4.wireOp",EDGE,"E92.6"),sQuery(id+"F4.wireOp",EDGE,"E92.7"),sQuery(id+"F4.wireOp",EDGE,"E92.8"),sQuery(id+"F4.wireOp",EDGE,"E92.9"),sQuery(id+"F4.wireOp",EDGE,"E92.10"),sQuery(id+"F4.wireOp",EDGE,"E92.11"),sQuery(id+"F4.wireOp",EDGE,"E92.12"),sQuery(id+"F4.wireOp",EDGE,"E92.13"),sQuery(id+"F4.wireOp",EDGE,"E92.14"),sQuery(id+"F4.wireOp",EDGE,"E92.15"),sQuery(id+"F4.wireOp",EDGE,"E92.16"),sQuery(id+"F4.wireOp",EDGE,"E92.17"),sQuery(id+"F4.wireOp",EDGE,"E93"),sQuery(id+"F4.wireOp",EDGE,"E94")])],"isStart":false})]});
            fillet(context, id + "F13", {"entities" : qUnion([Q0, Q1, Q2, Q3, Q4, Q5, Q6, Q7, Q8, Q9, Q10, Q11, Q12, Q13, Q14, Q15, Q16, Q17, Q18, Q19]), "radius" : 7.62 * mm, "tangentPropagation" : true, "allowEdgeOverflow" : false});
        }
    });
